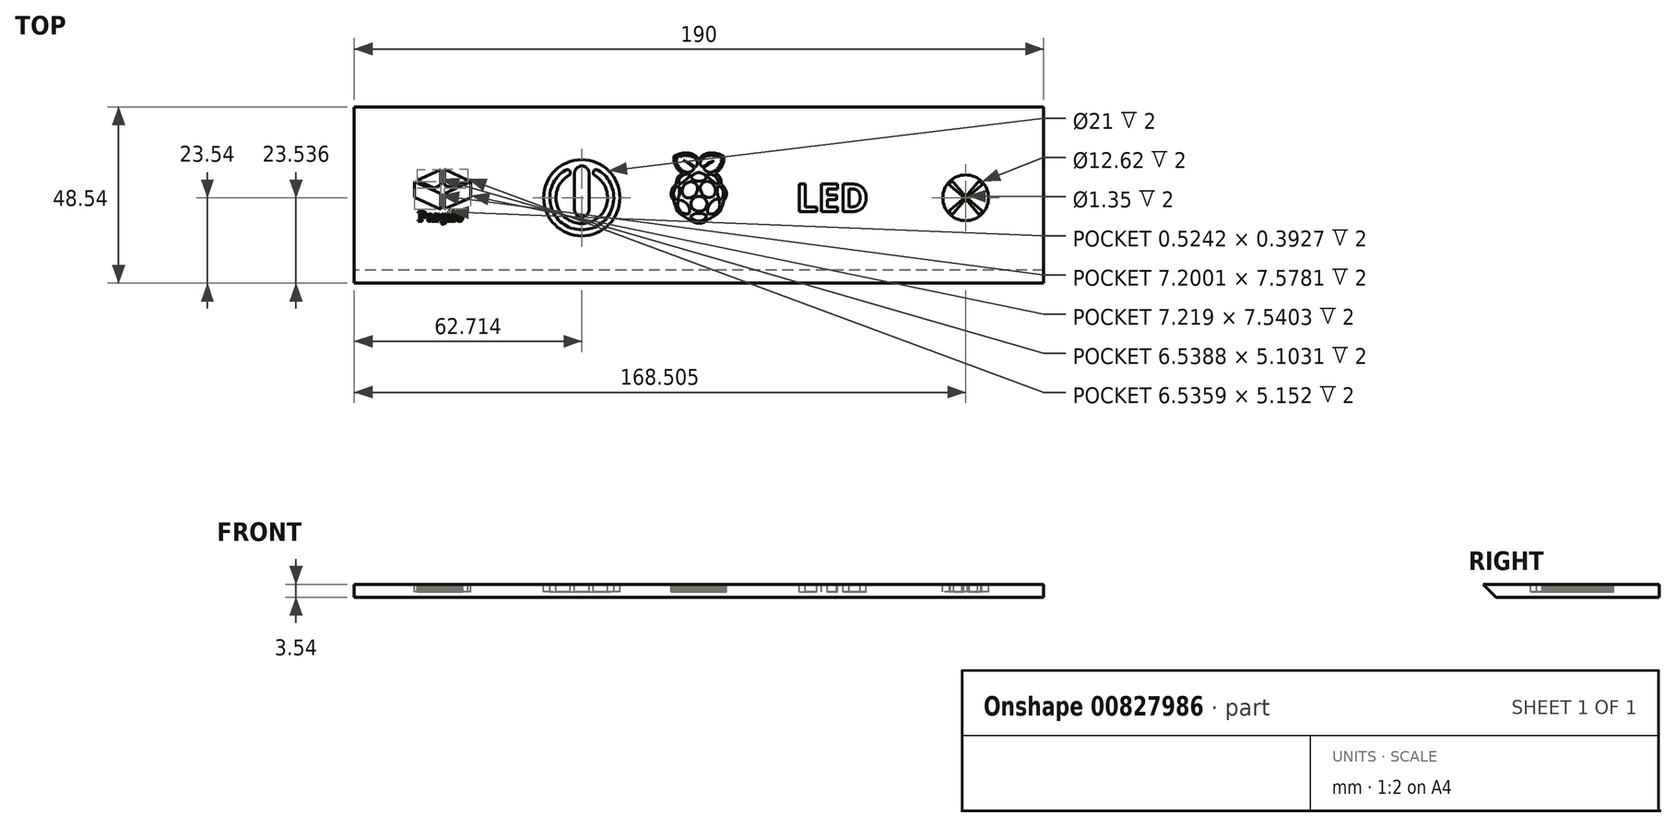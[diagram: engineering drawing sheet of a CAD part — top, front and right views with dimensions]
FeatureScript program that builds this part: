
annotation { "Feature Type Name" : "Feature", "Feature Type Description" : "" }
export const myFeature = defineFeature(function(context is Context, id is Id, definition is map)
    precondition{}
    {
        {
            var Q0;
            Q0=qCreatedBy(makeId("Top.planeOp"),FACE);
            var sketch = newSketch(context, id + "F0", { "sketchPlane" : qUnion([Q0])});
            skLineSegment(sketch, "E0.bottom", {"start": v(95, -25) * mm, "end": v(-95, -25) * mm});
            skLineSegment(sketch, "E0.top", {"start": v(95, 25) * mm, "end": v(-95, 25) * mm});
            skLineSegment(sketch, "E0.left", {"start": v(95, -25) * mm, "end": v(95, 25) * mm});
            skLineSegment(sketch, "E0.right", {"start": v(-95, -25) * mm, "end": v(-95, 25) * mm});
            skPoint(sketch, "E1.endSnap0", {"position": v(-58.55, -14.96) * mm});
            skSolve(sketch);
        }
        {
            var Q0;
            Q0=makeQuery(id+"F0.imprint","IMPRINT",FACE,{"disambiguationData":[TD([[makeQuery(id+"F0.imprint","IMPRINT",EDGE,{"derivedFrom":sQuery(id+"F0.wireOp",EDGE,"E0.bottom")}),-1.0]])]});
            extrude(context, id + "F1", {"entities" : qUnion([Q0]), "depth" : 3.54 * mm, "offsetDistance" : 25 * mm});
        }
        {
            var Q0;
            Q0=makeQuery(id+"F1.opExtrude","CAP_EDGE",EDGE,{"disambiguationData":[OSD([sQuery(id+"F0.wireOp",EDGE,"E0.bottom")])],"isStart":true});
            chamfer(context, id + "F2", {"entities" : qUnion([Q0]), "width" : 5 * mm, "tangentPropagation" : true});
        }
        {
            var Q0;
            Q0=makeQuery(id+"F1.opExtrude","CAP_FACE",FACE,{"disambiguationData":[OSD([sQuery(id+"F0.wireOp",EDGE,"E0.bottom"),sQuery(id+"F0.wireOp",EDGE,"E0.top"),sQuery(id+"F0.wireOp",EDGE,"E0.left"),sQuery(id+"F0.wireOp",EDGE,"E0.right")])],"isStart":false});
            var sketch = newSketch(context, id + "F3", { "sketchPlane" : qUnion([Q0])});
            skPoint(sketch, "E2", {"position": v(0, 6.13) * mm});
            skPoint(sketch, "E3", {"position": v(36.75, 0) * mm});
            skPoint(sketch, "E4", {"position": v(73.5, 0) * mm});
            skPoint(sketch, "E5", {"position": v(-70.53, 0) * mm});
            skPoint(sketch, "E6", {"position": v(-32.17, -0.8) * mm});
            skLineSegment(sketch, "E7", {"start": v(0.77, -6.95) * mm, "end": v(0.42, -7.01) * mm});
            skLineSegment(sketch, "E8", {"start": v(0.42, -7.01) * mm, "end": v(0.04, -7.03) * mm});
            skLineSegment(sketch, "E9", {"start": v(2.22, -6.14) * mm, "end": v(1.83, -6.45) * mm});
            skLineSegment(sketch, "E10", {"start": v(1.83, -6.45) * mm, "end": v(1.43, -6.7) * mm});
            skLineSegment(sketch, "E11", {"start": v(1.43, -6.7) * mm, "end": v(0.77, -6.95) * mm});
            skLineSegment(sketch, "E12", {"start": v(2.72, -5.84) * mm, "end": v(2.42, -6) * mm});
            skLineSegment(sketch, "E13", {"start": v(2.42, -6) * mm, "end": v(2.22, -6.14) * mm});
            skLineSegment(sketch, "E14", {"start": v(3.97, -5.13) * mm, "end": v(3.25, -5.58) * mm});
            skLineSegment(sketch, "E15", {"start": v(3.25, -5.58) * mm, "end": v(2.72, -5.84) * mm});
            skLineSegment(sketch, "E16", {"start": v(4.55, -4.78) * mm, "end": v(4.42, -4.85) * mm});
            skLineSegment(sketch, "E17", {"start": v(4.42, -4.85) * mm, "end": v(4.25, -4.95) * mm});
            skLineSegment(sketch, "E18", {"start": v(4.25, -4.95) * mm, "end": v(3.97, -5.13) * mm});
            skLineSegment(sketch, "E19", {"start": v(5.47, -4.1) * mm, "end": v(5.2, -4.35) * mm});
            skLineSegment(sketch, "E20", {"start": v(5.2, -4.35) * mm, "end": v(4.96, -4.54) * mm});
            skLineSegment(sketch, "E21", {"start": v(4.96, -4.54) * mm, "end": v(4.55, -4.78) * mm});
            skLineSegment(sketch, "E22", {"start": v(6.36, -2.47) * mm, "end": v(6.2, -2.98) * mm});
            skLineSegment(sketch, "E23", {"start": v(6.2, -2.98) * mm, "end": v(5.98, -3.45) * mm});
            skLineSegment(sketch, "E24", {"start": v(5.98, -3.45) * mm, "end": v(5.75, -3.8) * mm});
            skLineSegment(sketch, "E25", {"start": v(5.75, -3.8) * mm, "end": v(5.47, -4.1) * mm});
            skLineSegment(sketch, "E26", {"start": v(6.55, -1.8) * mm, "end": v(6.42, -2.2) * mm});
            skLineSegment(sketch, "E27", {"start": v(6.42, -2.2) * mm, "end": v(6.36, -2.47) * mm});
            skLineSegment(sketch, "E28", {"start": v(6.75, -1.16) * mm, "end": v(6.7, -1.31) * mm});
            skLineSegment(sketch, "E29", {"start": v(6.7, -1.31) * mm, "end": v(6.65, -1.5) * mm});
            skLineSegment(sketch, "E30", {"start": v(6.65, -1.5) * mm, "end": v(6.55, -1.8) * mm});
            skLineSegment(sketch, "E31", {"start": v(6.98, -0.7) * mm, "end": v(6.89, -0.82) * mm});
            skLineSegment(sketch, "E32", {"start": v(6.89, -0.82) * mm, "end": v(6.82, -0.94) * mm});
            skLineSegment(sketch, "E33", {"start": v(6.82, -0.94) * mm, "end": v(6.75, -1.16) * mm});
            skLineSegment(sketch, "E34", {"start": v(7.5, 0.37) * mm, "end": v(7.4, 0.07) * mm});
            skLineSegment(sketch, "E35", {"start": v(7.4, 0.07) * mm, "end": v(7.25, -0.25) * mm});
            skLineSegment(sketch, "E36", {"start": v(7.25, -0.25) * mm, "end": v(7.12, -0.49) * mm});
            skLineSegment(sketch, "E37", {"start": v(7.12, -0.49) * mm, "end": v(6.98, -0.7) * mm});
            skLineSegment(sketch, "E38", {"start": v(7.5, 1.8) * mm, "end": v(7.56, 1.42) * mm});
            skLineSegment(sketch, "E39", {"start": v(7.56, 1.42) * mm, "end": v(7.57, 0.99) * mm});
            skLineSegment(sketch, "E40", {"start": v(7.57, 0.99) * mm, "end": v(7.55, 0.65) * mm});
            skLineSegment(sketch, "E41", {"start": v(7.55, 0.65) * mm, "end": v(7.5, 0.37) * mm});
            skLineSegment(sketch, "E42", {"start": v(7.13, 2.68) * mm, "end": v(7.37, 2.2) * mm});
            skLineSegment(sketch, "E43", {"start": v(7.37, 2.2) * mm, "end": v(7.5, 1.8) * mm});
            skLineSegment(sketch, "E44", {"start": v(6.4, 3.5) * mm, "end": v(6.6, 3.33) * mm});
            skLineSegment(sketch, "E45", {"start": v(6.6, 3.33) * mm, "end": v(6.84, 3.08) * mm});
            skLineSegment(sketch, "E46", {"start": v(6.84, 3.08) * mm, "end": v(7, 2.87) * mm});
            skLineSegment(sketch, "E47", {"start": v(7, 2.87) * mm, "end": v(7.13, 2.68) * mm});
            skLineSegment(sketch, "E48", {"start": v(6.12, 4.2) * mm, "end": v(6.15, 3.9) * mm});
            skLineSegment(sketch, "E49", {"start": v(6.15, 3.9) * mm, "end": v(6.2, 3.71) * mm});
            skLineSegment(sketch, "E50", {"start": v(6.2, 3.71) * mm, "end": v(6.4, 3.5) * mm});
            skLineSegment(sketch, "E51", {"start": v(4.66, 6.7) * mm, "end": v(5.12, 6.35) * mm});
            skLineSegment(sketch, "E52", {"start": v(5.12, 6.35) * mm, "end": v(5.5, 5.95) * mm});
            skLineSegment(sketch, "E53", {"start": v(5.5, 5.95) * mm, "end": v(5.8, 5.5) * mm});
            skLineSegment(sketch, "E54", {"start": v(5.8, 5.5) * mm, "end": v(6.02, 4.89) * mm});
            skLineSegment(sketch, "E55", {"start": v(6.02, 4.89) * mm, "end": v(6.12, 4.2) * mm});
            skLineSegment(sketch, "E56", {"start": v(4.5, 6.8) * mm, "end": v(4.66, 6.7) * mm});
            skLineSegment(sketch, "E57", {"start": v(4.7, 6.88) * mm, "end": v(4.5, 6.8) * mm});
            skLineSegment(sketch, "E58", {"start": v(5.04, 7.22) * mm, "end": v(4.9, 7) * mm});
            skLineSegment(sketch, "E59", {"start": v(4.9, 7) * mm, "end": v(4.7, 6.88) * mm});
            skLineSegment(sketch, "E60", {"start": v(5.23, 7.35) * mm, "end": v(5.09, 7.28) * mm});
            skLineSegment(sketch, "E61", {"start": v(5.09, 7.28) * mm, "end": v(5.04, 7.22) * mm});
            skLineSegment(sketch, "E62", {"start": v(5.67, 7.78) * mm, "end": v(5.6, 7.63) * mm});
            skLineSegment(sketch, "E63", {"start": v(5.6, 7.63) * mm, "end": v(5.48, 7.5) * mm});
            skLineSegment(sketch, "E64", {"start": v(5.48, 7.5) * mm, "end": v(5.23, 7.35) * mm});
            skLineSegment(sketch, "E65", {"start": v(5.8, 7.95) * mm, "end": v(5.71, 7.87) * mm});
            skLineSegment(sketch, "E66", {"start": v(5.71, 7.87) * mm, "end": v(5.67, 7.78) * mm});
            skLineSegment(sketch, "E67", {"start": v(6.2, 8.49) * mm, "end": v(6.13, 8.32) * mm});
            skLineSegment(sketch, "E68", {"start": v(6.13, 8.32) * mm, "end": v(6.01, 8.15) * mm});
            skLineSegment(sketch, "E69", {"start": v(6.01, 8.15) * mm, "end": v(5.8, 7.95) * mm});
            skLineSegment(sketch, "E70", {"start": v(6.3, 8.7) * mm, "end": v(6.26, 8.66) * mm});
            skLineSegment(sketch, "E71", {"start": v(6.26, 8.66) * mm, "end": v(6.24, 8.61) * mm});
            skLineSegment(sketch, "E72", {"start": v(6.24, 8.61) * mm, "end": v(6.2, 8.49) * mm});
            skLineSegment(sketch, "E73", {"start": v(6.52, 9.16) * mm, "end": v(6.5, 9.01) * mm});
            skLineSegment(sketch, "E74", {"start": v(6.5, 9.01) * mm, "end": v(6.43, 8.86) * mm});
            skLineSegment(sketch, "E75", {"start": v(6.43, 8.86) * mm, "end": v(6.37, 8.76) * mm});
            skLineSegment(sketch, "E76", {"start": v(6.37, 8.76) * mm, "end": v(6.3, 8.7) * mm});
            skLineSegment(sketch, "E77", {"start": v(6.63, 9.47) * mm, "end": v(6.54, 9.3) * mm});
            skLineSegment(sketch, "E78", {"start": v(6.54, 9.3) * mm, "end": v(6.52, 9.16) * mm});
            skLineSegment(sketch, "E79", {"start": v(6.77, 9.96) * mm, "end": v(6.75, 9.7) * mm});
            skLineSegment(sketch, "E80", {"start": v(6.75, 9.7) * mm, "end": v(6.63, 9.47) * mm});
            skLineSegment(sketch, "E81", {"start": v(6.83, 10.21) * mm, "end": v(6.77, 10.06) * mm});
            skLineSegment(sketch, "E82", {"start": v(6.77, 10.06) * mm, "end": v(6.77, 9.96) * mm});
            skLineSegment(sketch, "E83", {"start": v(6.85, 10.75) * mm, "end": v(6.9, 10.45) * mm});
            skLineSegment(sketch, "E84", {"start": v(6.9, 10.45) * mm, "end": v(6.83, 10.21) * mm});
            skLineSegment(sketch, "E85", {"start": v(6.81, 10.96) * mm, "end": v(6.8, 10.86) * mm});
            skLineSegment(sketch, "E86", {"start": v(6.8, 10.86) * mm, "end": v(6.85, 10.75) * mm});
            skLineSegment(sketch, "E87", {"start": v(6.78, 11.48) * mm, "end": v(6.82, 11.35) * mm});
            skLineSegment(sketch, "E88", {"start": v(6.82, 11.35) * mm, "end": v(6.84, 11.2) * mm});
            skLineSegment(sketch, "E89", {"start": v(6.84, 11.2) * mm, "end": v(6.81, 10.96) * mm});
            skLineSegment(sketch, "E90", {"start": v(6.29, 11.71) * mm, "end": v(6.6, 11.63) * mm});
            skLineSegment(sketch, "E91", {"start": v(6.6, 11.63) * mm, "end": v(6.78, 11.48) * mm});
            skLineSegment(sketch, "E92", {"start": v(6.08, 11.78) * mm, "end": v(6.17, 11.73) * mm});
            skLineSegment(sketch, "E93", {"start": v(6.17, 11.73) * mm, "end": v(6.29, 11.71) * mm});
            skLineSegment(sketch, "E94", {"start": v(5.5, 12) * mm, "end": v(5.88, 11.92) * mm});
            skLineSegment(sketch, "E95", {"start": v(5.88, 11.92) * mm, "end": v(6.08, 11.78) * mm});
            skLineSegment(sketch, "E96", {"start": v(5.18, 12.06) * mm, "end": v(5.24, 12.04) * mm});
            skLineSegment(sketch, "E97", {"start": v(5.24, 12.04) * mm, "end": v(5.31, 12.02) * mm});
            skLineSegment(sketch, "E98", {"start": v(5.31, 12.02) * mm, "end": v(5.5, 12) * mm});
            skLineSegment(sketch, "E99", {"start": v(4.75, 12.2) * mm, "end": v(5.02, 12.15) * mm});
            skLineSegment(sketch, "E100", {"start": v(5.02, 12.15) * mm, "end": v(5.18, 12.06) * mm});
            skLineSegment(sketch, "E101", {"start": v(4.5, 12.27) * mm, "end": v(4.64, 12.22) * mm});
            skLineSegment(sketch, "E102", {"start": v(4.64, 12.22) * mm, "end": v(4.75, 12.2) * mm});
            skLineSegment(sketch, "E103", {"start": v(3.87, 12.3) * mm, "end": v(4.03, 12.33) * mm});
            skLineSegment(sketch, "E104", {"start": v(4.03, 12.33) * mm, "end": v(4.23, 12.33) * mm});
            skLineSegment(sketch, "E105", {"start": v(4.23, 12.33) * mm, "end": v(4.37, 12.3) * mm});
            skLineSegment(sketch, "E106", {"start": v(4.37, 12.3) * mm, "end": v(4.5, 12.27) * mm});
            skLineSegment(sketch, "E107", {"start": v(3.7, 12.32) * mm, "end": v(3.8, 12.28) * mm});
            skLineSegment(sketch, "E108", {"start": v(3.8, 12.28) * mm, "end": v(3.87, 12.3) * mm});
            skLineSegment(sketch, "E109", {"start": v(3.12, 12.31) * mm, "end": v(3.27, 12.35) * mm});
            skLineSegment(sketch, "E110", {"start": v(3.27, 12.35) * mm, "end": v(3.46, 12.36) * mm});
            skLineSegment(sketch, "E111", {"start": v(3.46, 12.36) * mm, "end": v(3.6, 12.35) * mm});
            skLineSegment(sketch, "E112", {"start": v(3.6, 12.35) * mm, "end": v(3.7, 12.32) * mm});
            skLineSegment(sketch, "E113", {"start": v(2.74, 12.26) * mm, "end": v(2.99, 12.28) * mm});
            skLineSegment(sketch, "E114", {"start": v(2.99, 12.28) * mm, "end": v(3.12, 12.31) * mm});
            skLineSegment(sketch, "E115", {"start": v(2.34, 12.19) * mm, "end": v(2.53, 12.26) * mm});
            skLineSegment(sketch, "E116", {"start": v(2.53, 12.26) * mm, "end": v(2.74, 12.26) * mm});
            skLineSegment(sketch, "E117", {"start": v(2.08, 12.12) * mm, "end": v(2.22, 12.13) * mm});
            skLineSegment(sketch, "E118", {"start": v(2.22, 12.13) * mm, "end": v(2.34, 12.19) * mm});
            skLineSegment(sketch, "E119", {"start": v(1.52, 11.92) * mm, "end": v(1.83, 12.1) * mm});
            skLineSegment(sketch, "E120", {"start": v(1.83, 12.1) * mm, "end": v(2.08, 12.12) * mm});
            skLineSegment(sketch, "E121", {"start": v(1.24, 11.78) * mm, "end": v(1.39, 11.81) * mm});
            skLineSegment(sketch, "E122", {"start": v(1.39, 11.81) * mm, "end": v(1.52, 11.92) * mm});
            skLineSegment(sketch, "E123", {"start": v(0.07, 10.47) * mm, "end": v(0.35, 11.02) * mm});
            skLineSegment(sketch, "E124", {"start": v(0.35, 11.02) * mm, "end": v(0.7, 11.46) * mm});
            skLineSegment(sketch, "E125", {"start": v(0.7, 11.46) * mm, "end": v(1.02, 11.71) * mm});
            skLineSegment(sketch, "E126", {"start": v(1.02, 11.71) * mm, "end": v(1.24, 11.78) * mm});
            skLineSegment(sketch, "E127", {"start": v(-0.07, 10.3) * mm, "end": v(-0.07, 10.27) * mm});
            skLineSegment(sketch, "E128", {"start": v(-0.07, 10.27) * mm, "end": v(-0.06, 10.26) * mm});
            skLineSegment(sketch, "E129", {"start": v(-0.06, 10.26) * mm, "end": v(-0.05, 10.25) * mm});
            skLineSegment(sketch, "E130", {"start": v(-0.05, 10.25) * mm, "end": v(-0.04, 10.26) * mm});
            skLineSegment(sketch, "E131", {"start": v(-0.04, 10.26) * mm, "end": v(0.01, 10.35) * mm});
            skLineSegment(sketch, "E132", {"start": v(0.01, 10.35) * mm, "end": v(0.07, 10.47) * mm});
            skLineSegment(sketch, "E133", {"start": v(-0.6, 11.27) * mm, "end": v(-0.5, 11.11) * mm});
            skLineSegment(sketch, "E134", {"start": v(-0.5, 11.11) * mm, "end": v(-0.36, 10.9) * mm});
            skLineSegment(sketch, "E135", {"start": v(-0.36, 10.9) * mm, "end": v(-0.23, 10.67) * mm});
            skLineSegment(sketch, "E136", {"start": v(-0.23, 10.67) * mm, "end": v(-0.1, 10.42) * mm});
            skLineSegment(sketch, "E137", {"start": v(-0.1, 10.42) * mm, "end": v(-0.08, 10.34) * mm});
            skLineSegment(sketch, "E138", {"start": v(-0.08, 10.34) * mm, "end": v(-0.07, 10.3) * mm});
            skLineSegment(sketch, "E139", {"start": v(-1.31, 11.78) * mm, "end": v(-1.14, 11.73) * mm});
            skLineSegment(sketch, "E140", {"start": v(-1.14, 11.73) * mm, "end": v(-0.94, 11.6) * mm});
            skLineSegment(sketch, "E141", {"start": v(-0.94, 11.6) * mm, "end": v(-0.6, 11.27) * mm});
            skLineSegment(sketch, "E142", {"start": v(-1.6, 11.92) * mm, "end": v(-1.5, 11.84) * mm});
            skLineSegment(sketch, "E143", {"start": v(-1.5, 11.84) * mm, "end": v(-1.43, 11.8) * mm});
            skLineSegment(sketch, "E144", {"start": v(-1.43, 11.8) * mm, "end": v(-1.31, 11.78) * mm});
            skLineSegment(sketch, "E145", {"start": v(-2.14, 12.13) * mm, "end": v(-1.83, 12.08) * mm});
            skLineSegment(sketch, "E146", {"start": v(-1.83, 12.08) * mm, "end": v(-1.6, 11.92) * mm});
            skLineSegment(sketch, "E147", {"start": v(-2.42, 12.2) * mm, "end": v(-2.25, 12.13) * mm});
            skLineSegment(sketch, "E148", {"start": v(-2.25, 12.13) * mm, "end": v(-2.14, 12.13) * mm});
            skLineSegment(sketch, "E149", {"start": v(-2.8, 12.26) * mm, "end": v(-2.67, 12.26) * mm});
            skLineSegment(sketch, "E150", {"start": v(-2.67, 12.26) * mm, "end": v(-2.57, 12.25) * mm});
            skLineSegment(sketch, "E151", {"start": v(-2.57, 12.25) * mm, "end": v(-2.42, 12.2) * mm});
            skLineSegment(sketch, "E152", {"start": v(-3.16, 12.3) * mm, "end": v(-2.98, 12.26) * mm});
            skLineSegment(sketch, "E153", {"start": v(-2.98, 12.26) * mm, "end": v(-2.8, 12.26) * mm});
            skLineSegment(sketch, "E154", {"start": v(-3.77, 12.32) * mm, "end": v(-3.62, 12.36) * mm});
            skLineSegment(sketch, "E155", {"start": v(-3.62, 12.36) * mm, "end": v(-3.43, 12.36) * mm});
            skLineSegment(sketch, "E156", {"start": v(-3.43, 12.36) * mm, "end": v(-3.16, 12.3) * mm});
            skLineSegment(sketch, "E157", {"start": v(-3.96, 12.3) * mm, "end": v(-3.85, 12.29) * mm});
            skLineSegment(sketch, "E158", {"start": v(-3.85, 12.29) * mm, "end": v(-3.77, 12.32) * mm});
            skLineSegment(sketch, "E159", {"start": v(-4.6, 12.25) * mm, "end": v(-4.43, 12.3) * mm});
            skLineSegment(sketch, "E160", {"start": v(-4.43, 12.3) * mm, "end": v(-4.25, 12.33) * mm});
            skLineSegment(sketch, "E161", {"start": v(-4.25, 12.33) * mm, "end": v(-4.09, 12.33) * mm});
            skLineSegment(sketch, "E162", {"start": v(-4.09, 12.33) * mm, "end": v(-3.96, 12.3) * mm});
            skLineSegment(sketch, "E163", {"start": v(-4.8, 12.2) * mm, "end": v(-4.68, 12.21) * mm});
            skLineSegment(sketch, "E164", {"start": v(-4.68, 12.21) * mm, "end": v(-4.6, 12.25) * mm});
            skLineSegment(sketch, "E165", {"start": v(-5.24, 12.07) * mm, "end": v(-5, 12.18) * mm});
            skLineSegment(sketch, "E166", {"start": v(-5, 12.18) * mm, "end": v(-4.8, 12.2) * mm});
            skLineSegment(sketch, "E167", {"start": v(-5.51, 12) * mm, "end": v(-5.33, 12.03) * mm});
            skLineSegment(sketch, "E168", {"start": v(-5.33, 12.03) * mm, "end": v(-5.24, 12.07) * mm});
            skLineSegment(sketch, "E169", {"start": v(-6.09, 11.83) * mm, "end": v(-5.8, 11.98) * mm});
            skLineSegment(sketch, "E170", {"start": v(-5.8, 11.98) * mm, "end": v(-5.51, 12) * mm});
            skLineSegment(sketch, "E171", {"start": v(-6.37, 11.71) * mm, "end": v(-6.22, 11.75) * mm});
            skLineSegment(sketch, "E172", {"start": v(-6.22, 11.75) * mm, "end": v(-6.09, 11.83) * mm});
            skLineSegment(sketch, "E173", {"start": v(-6.85, 11.48) * mm, "end": v(-6.76, 11.58) * mm});
            skLineSegment(sketch, "E174", {"start": v(-6.76, 11.58) * mm, "end": v(-6.62, 11.66) * mm});
            skLineSegment(sketch, "E175", {"start": v(-6.62, 11.66) * mm, "end": v(-6.37, 11.71) * mm});
            skLineSegment(sketch, "E176", {"start": v(-6.89, 10.95) * mm, "end": v(-6.92, 11.1) * mm});
            skLineSegment(sketch, "E177", {"start": v(-6.92, 11.1) * mm, "end": v(-6.91, 11.26) * mm});
            skLineSegment(sketch, "E178", {"start": v(-6.91, 11.26) * mm, "end": v(-6.85, 11.48) * mm});
            skLineSegment(sketch, "E179", {"start": v(-6.92, 10.74) * mm, "end": v(-6.87, 10.87) * mm});
            skLineSegment(sketch, "E180", {"start": v(-6.87, 10.87) * mm, "end": v(-6.89, 10.95) * mm});
            skLineSegment(sketch, "E181", {"start": v(-6.9, 10.22) * mm, "end": v(-6.98, 10.52) * mm});
            skLineSegment(sketch, "E182", {"start": v(-6.98, 10.52) * mm, "end": v(-6.92, 10.74) * mm});
            skLineSegment(sketch, "E183", {"start": v(-6.84, 9.95) * mm, "end": v(-6.84, 10.08) * mm});
            skLineSegment(sketch, "E184", {"start": v(-6.84, 10.08) * mm, "end": v(-6.9, 10.22) * mm});
            skLineSegment(sketch, "E185", {"start": v(-6.69, 9.45) * mm, "end": v(-6.83, 9.75) * mm});
            skLineSegment(sketch, "E186", {"start": v(-6.83, 9.75) * mm, "end": v(-6.84, 9.95) * mm});
            skLineSegment(sketch, "E187", {"start": v(-6.6, 9.18) * mm, "end": v(-6.62, 9.33) * mm});
            skLineSegment(sketch, "E188", {"start": v(-6.62, 9.33) * mm, "end": v(-6.69, 9.45) * mm});
            skLineSegment(sketch, "E189", {"start": v(-6.39, 8.73) * mm, "end": v(-6.55, 8.97) * mm});
            skLineSegment(sketch, "E190", {"start": v(-6.55, 8.97) * mm, "end": v(-6.6, 9.18) * mm});
            skLineSegment(sketch, "E191", {"start": v(-6.27, 8.53) * mm, "end": v(-6.3, 8.64) * mm});
            skLineSegment(sketch, "E192", {"start": v(-6.3, 8.64) * mm, "end": v(-6.39, 8.73) * mm});
            skLineSegment(sketch, "E193", {"start": v(-5.82, 7.92) * mm, "end": v(-6, 8.06) * mm});
            skLineSegment(sketch, "E194", {"start": v(-6, 8.06) * mm, "end": v(-6.16, 8.24) * mm});
            skLineSegment(sketch, "E195", {"start": v(-6.16, 8.24) * mm, "end": v(-6.24, 8.4) * mm});
            skLineSegment(sketch, "E196", {"start": v(-6.24, 8.4) * mm, "end": v(-6.27, 8.53) * mm});
            skLineSegment(sketch, "E197", {"start": v(-5.75, 7.83) * mm, "end": v(-5.77, 7.89) * mm});
            skLineSegment(sketch, "E198", {"start": v(-5.77, 7.89) * mm, "end": v(-5.82, 7.92) * mm});
            skLineSegment(sketch, "E199", {"start": v(-5.23, 7.32) * mm, "end": v(-5.43, 7.4) * mm});
            skLineSegment(sketch, "E200", {"start": v(-5.43, 7.4) * mm, "end": v(-5.61, 7.56) * mm});
            skLineSegment(sketch, "E201", {"start": v(-5.61, 7.56) * mm, "end": v(-5.71, 7.7) * mm});
            skLineSegment(sketch, "E202", {"start": v(-5.71, 7.7) * mm, "end": v(-5.75, 7.83) * mm});
            skLineSegment(sketch, "E203", {"start": v(-5.08, 7.16) * mm, "end": v(-5.16, 7.28) * mm});
            skLineSegment(sketch, "E204", {"start": v(-5.16, 7.28) * mm, "end": v(-5.23, 7.32) * mm});
            skLineSegment(sketch, "E205", {"start": v(-4.64, 6.83) * mm, "end": v(-4.8, 6.89) * mm});
            skLineSegment(sketch, "E206", {"start": v(-4.8, 6.89) * mm, "end": v(-4.93, 6.98) * mm});
            skLineSegment(sketch, "E207", {"start": v(-4.93, 6.98) * mm, "end": v(-5.08, 7.16) * mm});
            skLineSegment(sketch, "E208", {"start": v(-4.84, 6.62) * mm, "end": v(-4.65, 6.75) * mm});
            skLineSegment(sketch, "E209", {"start": v(-4.65, 6.75) * mm, "end": v(-4.6, 6.8) * mm});
            skLineSegment(sketch, "E210", {"start": v(-4.6, 6.8) * mm, "end": v(-4.6, 6.8) * mm});
            skLineSegment(sketch, "E211", {"start": v(-4.6, 6.8) * mm, "end": v(-4.6, 6.81) * mm});
            skLineSegment(sketch, "E212", {"start": v(-4.6, 6.81) * mm, "end": v(-4.62, 6.82) * mm});
            skLineSegment(sketch, "E213", {"start": v(-4.62, 6.82) * mm, "end": v(-4.64, 6.83) * mm});
            skLineSegment(sketch, "E214", {"start": v(-5.76, 5.7) * mm, "end": v(-5.56, 5.96) * mm});
            skLineSegment(sketch, "E215", {"start": v(-5.56, 5.96) * mm, "end": v(-5.3, 6.24) * mm});
            skLineSegment(sketch, "E216", {"start": v(-5.3, 6.24) * mm, "end": v(-5.06, 6.45) * mm});
            skLineSegment(sketch, "E217", {"start": v(-5.06, 6.45) * mm, "end": v(-4.84, 6.62) * mm});
            skLineSegment(sketch, "E218", {"start": v(-6.2, 4.15) * mm, "end": v(-6.14, 4.64) * mm});
            skLineSegment(sketch, "E219", {"start": v(-6.14, 4.64) * mm, "end": v(-6.04, 5.08) * mm});
            skLineSegment(sketch, "E220", {"start": v(-6.04, 5.08) * mm, "end": v(-5.76, 5.7) * mm});
            skLineSegment(sketch, "E221", {"start": v(-6.5, 3.5) * mm, "end": v(-6.34, 3.62) * mm});
            skLineSegment(sketch, "E222", {"start": v(-6.34, 3.62) * mm, "end": v(-6.25, 3.77) * mm});
            skLineSegment(sketch, "E223", {"start": v(-6.25, 3.77) * mm, "end": v(-6.21, 3.93) * mm});
            skLineSegment(sketch, "E224", {"start": v(-6.21, 3.93) * mm, "end": v(-6.2, 4.15) * mm});
            skLineSegment(sketch, "E225", {"start": v(-7.57, 1.76) * mm, "end": v(-7.37, 2.34) * mm});
            skLineSegment(sketch, "E226", {"start": v(-7.37, 2.34) * mm, "end": v(-7.08, 2.86) * mm});
            skLineSegment(sketch, "E227", {"start": v(-7.08, 2.86) * mm, "end": v(-6.8, 3.21) * mm});
            skLineSegment(sketch, "E228", {"start": v(-6.8, 3.21) * mm, "end": v(-6.5, 3.5) * mm});
            skLineSegment(sketch, "E229", {"start": v(-7.57, 0.39) * mm, "end": v(-7.63, 0.75) * mm});
            skLineSegment(sketch, "E230", {"start": v(-7.63, 0.75) * mm, "end": v(-7.65, 1.16) * mm});
            skLineSegment(sketch, "E231", {"start": v(-7.65, 1.16) * mm, "end": v(-7.62, 1.47) * mm});
            skLineSegment(sketch, "E232", {"start": v(-7.62, 1.47) * mm, "end": v(-7.57, 1.76) * mm});
            skLineSegment(sketch, "E233", {"start": v(-7.07, -0.66) * mm, "end": v(-7.4, -0.09) * mm});
            skLineSegment(sketch, "E234", {"start": v(-7.4, -0.09) * mm, "end": v(-7.57, 0.39) * mm});
            skLineSegment(sketch, "E235", {"start": v(-6.8, -1.22) * mm, "end": v(-6.86, -1.04) * mm});
            skLineSegment(sketch, "E236", {"start": v(-6.86, -1.04) * mm, "end": v(-6.92, -0.9) * mm});
            skLineSegment(sketch, "E237", {"start": v(-6.92, -0.9) * mm, "end": v(-7.07, -0.66) * mm});
            skLineSegment(sketch, "E238", {"start": v(-6.6, -1.84) * mm, "end": v(-6.73, -1.48) * mm});
            skLineSegment(sketch, "E239", {"start": v(-6.73, -1.48) * mm, "end": v(-6.8, -1.22) * mm});
            skLineSegment(sketch, "E240", {"start": v(-6.43, -2.47) * mm, "end": v(-6.47, -2.3) * mm});
            skLineSegment(sketch, "E241", {"start": v(-6.47, -2.3) * mm, "end": v(-6.52, -2.11) * mm});
            skLineSegment(sketch, "E242", {"start": v(-6.52, -2.11) * mm, "end": v(-6.6, -1.84) * mm});
            skLineSegment(sketch, "E243", {"start": v(-4.62, -4.78) * mm, "end": v(-5.1, -4.5) * mm});
            skLineSegment(sketch, "E244", {"start": v(-5.1, -4.5) * mm, "end": v(-5.53, -4.14) * mm});
            skLineSegment(sketch, "E245", {"start": v(-5.53, -4.14) * mm, "end": v(-5.89, -3.7) * mm});
            skLineSegment(sketch, "E246", {"start": v(-5.89, -3.7) * mm, "end": v(-6.22, -3.12) * mm});
            skLineSegment(sketch, "E247", {"start": v(-6.22, -3.12) * mm, "end": v(-6.43, -2.47) * mm});
            skLineSegment(sketch, "E248", {"start": v(-4.14, -5.07) * mm, "end": v(-4.42, -4.89) * mm});
            skLineSegment(sketch, "E249", {"start": v(-4.42, -4.89) * mm, "end": v(-4.62, -4.78) * mm});
            skLineSegment(sketch, "E250", {"start": v(-2.81, -5.83) * mm, "end": v(-3.17, -5.66) * mm});
            skLineSegment(sketch, "E251", {"start": v(-3.17, -5.66) * mm, "end": v(-3.55, -5.45) * mm});
            skLineSegment(sketch, "E252", {"start": v(-3.55, -5.45) * mm, "end": v(-4.14, -5.07) * mm});
            skLineSegment(sketch, "E253", {"start": v(-2.26, -6.17) * mm, "end": v(-2.52, -5.97) * mm});
            skLineSegment(sketch, "E254", {"start": v(-2.52, -5.97) * mm, "end": v(-2.65, -5.9) * mm});
            skLineSegment(sketch, "E255", {"start": v(-2.65, -5.9) * mm, "end": v(-2.81, -5.83) * mm});
            skLineSegment(sketch, "E256", {"start": v(-0.5, -7.02) * mm, "end": v(-1.04, -6.9) * mm});
            skLineSegment(sketch, "E257", {"start": v(-1.04, -6.9) * mm, "end": v(-1.55, -6.67) * mm});
            skLineSegment(sketch, "E258", {"start": v(-1.55, -6.67) * mm, "end": v(-1.92, -6.44) * mm});
            skLineSegment(sketch, "E259", {"start": v(-1.92, -6.44) * mm, "end": v(-2.26, -6.17) * mm});
            skLineSegment(sketch, "E260", {"start": v(0.04, -7.03) * mm, "end": v(-0.16, -7.03) * mm});
            skLineSegment(sketch, "E261", {"start": v(-0.16, -7.03) * mm, "end": v(-0.34, -7.03) * mm});
            skLineSegment(sketch, "E262", {"start": v(-0.34, -7.03) * mm, "end": v(-0.45, -7.03) * mm});
            skLineSegment(sketch, "E263", {"start": v(-0.45, -7.03) * mm, "end": v(-0.5, -7.02) * mm});
            skLineSegment(sketch, "E264", {"start": v(1.43, -5.93) * mm, "end": v(1.01, -6.18) * mm});
            skLineSegment(sketch, "E265", {"start": v(1.01, -6.18) * mm, "end": v(0.6, -6.34) * mm});
            skLineSegment(sketch, "E266", {"start": v(0.6, -6.34) * mm, "end": v(0.27, -6.4) * mm});
            skLineSegment(sketch, "E267", {"start": v(0.27, -6.4) * mm, "end": v(-0.08, -6.43) * mm});
            skLineSegment(sketch, "E268", {"start": v(-0.08, -6.43) * mm, "end": v(-0.42, -6.4) * mm});
            skLineSegment(sketch, "E269", {"start": v(-0.42, -6.4) * mm, "end": v(-0.62, -6.38) * mm});
            skLineSegment(sketch, "E270", {"start": v(-0.62, -6.38) * mm, "end": v(-1.06, -6.22) * mm});
            skLineSegment(sketch, "E271", {"start": v(-1.06, -6.22) * mm, "end": v(-1.47, -6) * mm});
            skLineSegment(sketch, "E272", {"start": v(-1.47, -6) * mm, "end": v(-1.82, -5.76) * mm});
            skLineSegment(sketch, "E273", {"start": v(-1.82, -5.76) * mm, "end": v(-2, -5.58) * mm});
            skLineSegment(sketch, "E274", {"start": v(-2, -5.58) * mm, "end": v(-2.13, -5.41) * mm});
            skLineSegment(sketch, "E275", {"start": v(-2.13, -5.41) * mm, "end": v(-2.21, -5.17) * mm});
            skLineSegment(sketch, "E276", {"start": v(-2.21, -5.17) * mm, "end": v(-2.18, -5.02) * mm});
            skLineSegment(sketch, "E277", {"start": v(-2.18, -5.02) * mm, "end": v(-2.07, -4.88) * mm});
            skLineSegment(sketch, "E278", {"start": v(-2.07, -4.88) * mm, "end": v(-1.93, -4.78) * mm});
            skLineSegment(sketch, "E279", {"start": v(-1.93, -4.78) * mm, "end": v(-1.74, -4.67) * mm});
            skLineSegment(sketch, "E280", {"start": v(-1.74, -4.67) * mm, "end": v(-1.3, -4.5) * mm});
            skLineSegment(sketch, "E281", {"start": v(-1.3, -4.5) * mm, "end": v(-0.8, -4.39) * mm});
            skLineSegment(sketch, "E282", {"start": v(-0.8, -4.39) * mm, "end": v(0.09, -4.32) * mm});
            skLineSegment(sketch, "E283", {"start": v(0.09, -4.32) * mm, "end": v(0.83, -4.37) * mm});
            skLineSegment(sketch, "E284", {"start": v(0.83, -4.37) * mm, "end": v(1.46, -4.52) * mm});
            skLineSegment(sketch, "E285", {"start": v(1.46, -4.52) * mm, "end": v(1.71, -4.62) * mm});
            skLineSegment(sketch, "E286", {"start": v(1.71, -4.62) * mm, "end": v(1.91, -4.74) * mm});
            skLineSegment(sketch, "E287", {"start": v(1.91, -4.74) * mm, "end": v(2.05, -4.87) * mm});
            skLineSegment(sketch, "E288", {"start": v(2.05, -4.87) * mm, "end": v(2.12, -5) * mm});
            skLineSegment(sketch, "E289", {"start": v(2.12, -5) * mm, "end": v(2.12, -5.12) * mm});
            skLineSegment(sketch, "E290", {"start": v(2.12, -5.12) * mm, "end": v(2.07, -5.26) * mm});
            skLineSegment(sketch, "E291", {"start": v(2.07, -5.26) * mm, "end": v(1.9, -5.5) * mm});
            skLineSegment(sketch, "E292", {"start": v(1.9, -5.5) * mm, "end": v(1.7, -5.73) * mm});
            skLineSegment(sketch, "E293", {"start": v(1.7, -5.73) * mm, "end": v(1.43, -5.93) * mm});
            skLineSegment(sketch, "E294", {"start": v(5.2, -3.47) * mm, "end": v(4.71, -3.96) * mm});
            skLineSegment(sketch, "E295", {"start": v(4.71, -3.96) * mm, "end": v(4.17, -4.3) * mm});
            skLineSegment(sketch, "E296", {"start": v(4.17, -4.3) * mm, "end": v(3.73, -4.46) * mm});
            skLineSegment(sketch, "E297", {"start": v(3.73, -4.46) * mm, "end": v(3.27, -4.5) * mm});
            skLineSegment(sketch, "E298", {"start": v(3.27, -4.5) * mm, "end": v(3.07, -4.5) * mm});
            skLineSegment(sketch, "E299", {"start": v(3.07, -4.5) * mm, "end": v(2.94, -4.48) * mm});
            skLineSegment(sketch, "E300", {"start": v(2.94, -4.48) * mm, "end": v(2.67, -4.37) * mm});
            skLineSegment(sketch, "E301", {"start": v(2.67, -4.37) * mm, "end": v(2.48, -4.2) * mm});
            skLineSegment(sketch, "E302", {"start": v(2.48, -4.2) * mm, "end": v(2.4, -4) * mm});
            skLineSegment(sketch, "E303", {"start": v(2.4, -4) * mm, "end": v(2.34, -3.75) * mm});
            skLineSegment(sketch, "E304", {"start": v(2.34, -3.75) * mm, "end": v(2.35, -3.42) * mm});
            skLineSegment(sketch, "E305", {"start": v(2.35, -3.42) * mm, "end": v(2.4, -3.05) * mm});
            skLineSegment(sketch, "E306", {"start": v(2.4, -3.05) * mm, "end": v(2.52, -2.66) * mm});
            skLineSegment(sketch, "E307", {"start": v(2.52, -2.66) * mm, "end": v(2.71, -2.2) * mm});
            skLineSegment(sketch, "E308", {"start": v(2.71, -2.2) * mm, "end": v(2.96, -1.77) * mm});
            skLineSegment(sketch, "E309", {"start": v(2.96, -1.77) * mm, "end": v(3.28, -1.38) * mm});
            skLineSegment(sketch, "E310", {"start": v(3.28, -1.38) * mm, "end": v(3.7, -0.98) * mm});
            skLineSegment(sketch, "E311", {"start": v(3.7, -0.98) * mm, "end": v(4.03, -0.71) * mm});
            skLineSegment(sketch, "E312", {"start": v(4.03, -0.71) * mm, "end": v(4.34, -0.52) * mm});
            skLineSegment(sketch, "E313", {"start": v(4.34, -0.52) * mm, "end": v(4.73, -0.39) * mm});
            skLineSegment(sketch, "E314", {"start": v(4.73, -0.39) * mm, "end": v(5.08, -0.4) * mm});
            skLineSegment(sketch, "E315", {"start": v(5.08, -0.4) * mm, "end": v(5.3, -0.5) * mm});
            skLineSegment(sketch, "E316", {"start": v(5.3, -0.5) * mm, "end": v(5.48, -0.68) * mm});
            skLineSegment(sketch, "E317", {"start": v(5.48, -0.68) * mm, "end": v(5.62, -0.98) * mm});
            skLineSegment(sketch, "E318", {"start": v(5.62, -0.98) * mm, "end": v(5.72, -1.35) * mm});
            skLineSegment(sketch, "E319", {"start": v(5.72, -1.35) * mm, "end": v(5.75, -1.76) * mm});
            skLineSegment(sketch, "E320", {"start": v(5.75, -1.76) * mm, "end": v(5.73, -2.26) * mm});
            skLineSegment(sketch, "E321", {"start": v(5.73, -2.26) * mm, "end": v(5.62, -2.72) * mm});
            skLineSegment(sketch, "E322", {"start": v(5.62, -2.72) * mm, "end": v(5.54, -2.94) * mm});
            skLineSegment(sketch, "E323", {"start": v(5.54, -2.94) * mm, "end": v(5.45, -3.12) * mm});
            skLineSegment(sketch, "E324", {"start": v(5.45, -3.12) * mm, "end": v(5.34, -3.28) * mm});
            skLineSegment(sketch, "E325", {"start": v(5.34, -3.28) * mm, "end": v(5.2, -3.47) * mm});
            skLineSegment(sketch, "E326", {"start": v(-2.57, -3.8) * mm, "end": v(-2.68, -4.13) * mm});
            skLineSegment(sketch, "E327", {"start": v(-2.68, -4.13) * mm, "end": v(-2.88, -4.34) * mm});
            skLineSegment(sketch, "E328", {"start": v(-2.88, -4.34) * mm, "end": v(-3.12, -4.42) * mm});
            skLineSegment(sketch, "E329", {"start": v(-3.12, -4.42) * mm, "end": v(-3.45, -4.45) * mm});
            skLineSegment(sketch, "E330", {"start": v(-3.45, -4.45) * mm, "end": v(-3.76, -4.42) * mm});
            skLineSegment(sketch, "E331", {"start": v(-3.76, -4.42) * mm, "end": v(-3.96, -4.38) * mm});
            skLineSegment(sketch, "E332", {"start": v(-3.96, -4.38) * mm, "end": v(-4.48, -4.16) * mm});
            skLineSegment(sketch, "E333", {"start": v(-4.48, -4.16) * mm, "end": v(-4.97, -3.8) * mm});
            skLineSegment(sketch, "E334", {"start": v(-4.97, -3.8) * mm, "end": v(-5.29, -3.47) * mm});
            skLineSegment(sketch, "E335", {"start": v(-5.29, -3.47) * mm, "end": v(-5.53, -3.1) * mm});
            skLineSegment(sketch, "E336", {"start": v(-5.53, -3.1) * mm, "end": v(-5.7, -2.68) * mm});
            skLineSegment(sketch, "E337", {"start": v(-5.7, -2.68) * mm, "end": v(-5.82, -2.22) * mm});
            skLineSegment(sketch, "E338", {"start": v(-5.82, -2.22) * mm, "end": v(-5.87, -1.88) * mm});
            skLineSegment(sketch, "E339", {"start": v(-5.87, -1.88) * mm, "end": v(-5.87, -1.58) * mm});
            skLineSegment(sketch, "E340", {"start": v(-5.87, -1.58) * mm, "end": v(-5.79, -1.21) * mm});
            skLineSegment(sketch, "E341", {"start": v(-5.79, -1.21) * mm, "end": v(-5.65, -0.94) * mm});
            skLineSegment(sketch, "E342", {"start": v(-5.65, -0.94) * mm, "end": v(-5.44, -0.76) * mm});
            skLineSegment(sketch, "E343", {"start": v(-5.44, -0.76) * mm, "end": v(-5.11, -0.68) * mm});
            skLineSegment(sketch, "E344", {"start": v(-5.11, -0.68) * mm, "end": v(-4.7, -0.73) * mm});
            skLineSegment(sketch, "E345", {"start": v(-4.7, -0.73) * mm, "end": v(-4.36, -0.87) * mm});
            skLineSegment(sketch, "E346", {"start": v(-4.36, -0.87) * mm, "end": v(-4, -1.09) * mm});
            skLineSegment(sketch, "E347", {"start": v(-4, -1.09) * mm, "end": v(-3.63, -1.37) * mm});
            skLineSegment(sketch, "E348", {"start": v(-3.63, -1.37) * mm, "end": v(-3.25, -1.75) * mm});
            skLineSegment(sketch, "E349", {"start": v(-3.25, -1.75) * mm, "end": v(-2.96, -2.16) * mm});
            skLineSegment(sketch, "E350", {"start": v(-2.96, -2.16) * mm, "end": v(-2.74, -2.63) * mm});
            skLineSegment(sketch, "E351", {"start": v(-2.74, -2.63) * mm, "end": v(-2.6, -3.12) * mm});
            skLineSegment(sketch, "E352", {"start": v(-2.6, -3.12) * mm, "end": v(-2.56, -3.49) * mm});
            skLineSegment(sketch, "E353", {"start": v(-2.56, -3.49) * mm, "end": v(-2.57, -3.8) * mm});
            skLineSegment(sketch, "E354", {"start": v(2.19, -2.15) * mm, "end": v(2.02, -2.56) * mm});
            skLineSegment(sketch, "E355", {"start": v(2.02, -2.56) * mm, "end": v(1.77, -2.93) * mm});
            skLineSegment(sketch, "E356", {"start": v(1.77, -2.93) * mm, "end": v(1.44, -3.25) * mm});
            skLineSegment(sketch, "E357", {"start": v(1.44, -3.25) * mm, "end": v(0.98, -3.53) * mm});
            skLineSegment(sketch, "E358", {"start": v(0.98, -3.53) * mm, "end": v(0.47, -3.7) * mm});
            skLineSegment(sketch, "E359", {"start": v(0.47, -3.7) * mm, "end": v(0.21, -3.73) * mm});
            skLineSegment(sketch, "E360", {"start": v(0.21, -3.73) * mm, "end": v(-0.1, -3.73) * mm});
            skLineSegment(sketch, "E361", {"start": v(-0.1, -3.73) * mm, "end": v(-0.32, -3.71) * mm});
            skLineSegment(sketch, "E362", {"start": v(-0.32, -3.71) * mm, "end": v(-0.5, -3.69) * mm});
            skLineSegment(sketch, "E363", {"start": v(-0.5, -3.69) * mm, "end": v(-1.09, -3.47) * mm});
            skLineSegment(sketch, "E364", {"start": v(-1.09, -3.47) * mm, "end": v(-1.58, -3.12) * mm});
            skLineSegment(sketch, "E365", {"start": v(-1.58, -3.12) * mm, "end": v(-1.89, -2.76) * mm});
            skLineSegment(sketch, "E366", {"start": v(-1.89, -2.76) * mm, "end": v(-2.1, -2.34) * mm});
            skLineSegment(sketch, "E367", {"start": v(-2.1, -2.34) * mm, "end": v(-2.17, -2.07) * mm});
            skLineSegment(sketch, "E368", {"start": v(-2.17, -2.07) * mm, "end": v(-2.2, -1.74) * mm});
            skLineSegment(sketch, "E369", {"start": v(-2.2, -1.74) * mm, "end": v(-2.2, -1.48) * mm});
            skLineSegment(sketch, "E370", {"start": v(-2.2, -1.48) * mm, "end": v(-2.18, -1.26) * mm});
            skLineSegment(sketch, "E371", {"start": v(-2.18, -1.26) * mm, "end": v(-2.05, -0.88) * mm});
            skLineSegment(sketch, "E372", {"start": v(-2.05, -0.88) * mm, "end": v(-1.84, -0.53) * mm});
            skLineSegment(sketch, "E373", {"start": v(-1.84, -0.53) * mm, "end": v(-1.56, -0.22) * mm});
            skLineSegment(sketch, "E374", {"start": v(-1.56, -0.22) * mm, "end": v(-1.14, 0.08) * mm});
            skLineSegment(sketch, "E375", {"start": v(-1.14, 0.08) * mm, "end": v(-0.67, 0.29) * mm});
            skLineSegment(sketch, "E376", {"start": v(-0.67, 0.29) * mm, "end": v(-0.25, 0.37) * mm});
            skLineSegment(sketch, "E377", {"start": v(-0.25, 0.37) * mm, "end": v(0.2, 0.37) * mm});
            skLineSegment(sketch, "E378", {"start": v(0.2, 0.37) * mm, "end": v(0.55, 0.32) * mm});
            skLineSegment(sketch, "E379", {"start": v(0.55, 0.32) * mm, "end": v(0.88, 0.23) * mm});
            skLineSegment(sketch, "E380", {"start": v(0.88, 0.23) * mm, "end": v(1.37, -0.04) * mm});
            skLineSegment(sketch, "E381", {"start": v(1.37, -0.04) * mm, "end": v(1.78, -0.43) * mm});
            skLineSegment(sketch, "E382", {"start": v(1.78, -0.43) * mm, "end": v(2.03, -0.8) * mm});
            skLineSegment(sketch, "E383", {"start": v(2.03, -0.8) * mm, "end": v(2.18, -1.2) * mm});
            skLineSegment(sketch, "E384", {"start": v(2.18, -1.2) * mm, "end": v(2.22, -1.44) * mm});
            skLineSegment(sketch, "E385", {"start": v(2.22, -1.44) * mm, "end": v(2.23, -1.74) * mm});
            skLineSegment(sketch, "E386", {"start": v(2.23, -1.74) * mm, "end": v(2.22, -1.96) * mm});
            skLineSegment(sketch, "E387", {"start": v(2.22, -1.96) * mm, "end": v(2.19, -2.15) * mm});
            skLineSegment(sketch, "E388", {"start": v(-5.39, 1.02) * mm, "end": v(-5.52, 0.43) * mm});
            skLineSegment(sketch, "E389", {"start": v(-5.52, 0.43) * mm, "end": v(-5.7, -0.06) * mm});
            skLineSegment(sketch, "E390", {"start": v(-5.7, -0.06) * mm, "end": v(-5.84, -0.36) * mm});
            skLineSegment(sketch, "E391", {"start": v(-5.84, -0.36) * mm, "end": v(-5.98, -0.54) * mm});
            skLineSegment(sketch, "E392", {"start": v(-5.98, -0.54) * mm, "end": v(-6.2, -0.62) * mm});
            skLineSegment(sketch, "E393", {"start": v(-6.2, -0.62) * mm, "end": v(-6.38, -0.55) * mm});
            skLineSegment(sketch, "E394", {"start": v(-6.38, -0.55) * mm, "end": v(-6.48, -0.44) * mm});
            skLineSegment(sketch, "E395", {"start": v(-6.48, -0.44) * mm, "end": v(-6.6, -0.28) * mm});
            skLineSegment(sketch, "E396", {"start": v(-6.6, -0.28) * mm, "end": v(-6.78, 0.02) * mm});
            skLineSegment(sketch, "E397", {"start": v(-6.78, 0.02) * mm, "end": v(-6.94, 0.44) * mm});
            skLineSegment(sketch, "E398", {"start": v(-6.94, 0.44) * mm, "end": v(-7.02, 0.88) * mm});
            skLineSegment(sketch, "E399", {"start": v(-7.02, 0.88) * mm, "end": v(-7.02, 1.34) * mm});
            skLineSegment(sketch, "E400", {"start": v(-7.02, 1.34) * mm, "end": v(-6.92, 1.86) * mm});
            skLineSegment(sketch, "E401", {"start": v(-6.92, 1.86) * mm, "end": v(-6.72, 2.33) * mm});
            skLineSegment(sketch, "E402", {"start": v(-6.72, 2.33) * mm, "end": v(-6.46, 2.67) * mm});
            skLineSegment(sketch, "E403", {"start": v(-6.46, 2.67) * mm, "end": v(-6.15, 2.96) * mm});
            skLineSegment(sketch, "E404", {"start": v(-6.15, 2.96) * mm, "end": v(-5.9, 3.13) * mm});
            skLineSegment(sketch, "E405", {"start": v(-5.9, 3.13) * mm, "end": v(-5.73, 3.18) * mm});
            skLineSegment(sketch, "E406", {"start": v(-5.73, 3.18) * mm, "end": v(-5.6, 3.15) * mm});
            skLineSegment(sketch, "E407", {"start": v(-5.6, 3.15) * mm, "end": v(-5.5, 3.05) * mm});
            skLineSegment(sketch, "E408", {"start": v(-5.5, 3.05) * mm, "end": v(-5.37, 2.8) * mm});
            skLineSegment(sketch, "E409", {"start": v(-5.37, 2.8) * mm, "end": v(-5.33, 2.62) * mm});
            skLineSegment(sketch, "E410", {"start": v(-5.33, 2.62) * mm, "end": v(-5.31, 2.36) * mm});
            skLineSegment(sketch, "E411", {"start": v(-5.31, 2.36) * mm, "end": v(-5.31, 1.87) * mm});
            skLineSegment(sketch, "E412", {"start": v(-5.31, 1.87) * mm, "end": v(-5.34, 1.42) * mm});
            skLineSegment(sketch, "E413", {"start": v(-5.34, 1.42) * mm, "end": v(-5.39, 1.02) * mm});
            skLineSegment(sketch, "E414", {"start": v(6.51, 0.07) * mm, "end": v(6.36, -0.19) * mm});
            skLineSegment(sketch, "E415", {"start": v(6.36, -0.19) * mm, "end": v(6.18, -0.41) * mm});
            skLineSegment(sketch, "E416", {"start": v(6.18, -0.41) * mm, "end": v(6.03, -0.55) * mm});
            skLineSegment(sketch, "E417", {"start": v(6.03, -0.55) * mm, "end": v(5.95, -0.59) * mm});
            skLineSegment(sketch, "E418", {"start": v(5.95, -0.59) * mm, "end": v(5.86, -0.56) * mm});
            skLineSegment(sketch, "E419", {"start": v(5.86, -0.56) * mm, "end": v(5.78, -0.52) * mm});
            skLineSegment(sketch, "E420", {"start": v(5.78, -0.52) * mm, "end": v(5.66, -0.42) * mm});
            skLineSegment(sketch, "E421", {"start": v(5.66, -0.42) * mm, "end": v(5.54, -0.25) * mm});
            skLineSegment(sketch, "E422", {"start": v(5.54, -0.25) * mm, "end": v(5.37, 0.13) * mm});
            skLineSegment(sketch, "E423", {"start": v(5.37, 0.13) * mm, "end": v(5.23, 0.57) * mm});
            skLineSegment(sketch, "E424", {"start": v(5.23, 0.57) * mm, "end": v(5.12, 1.1) * mm});
            skLineSegment(sketch, "E425", {"start": v(5.12, 1.1) * mm, "end": v(5.07, 1.43) * mm});
            skLineSegment(sketch, "E426", {"start": v(5.07, 1.43) * mm, "end": v(5.05, 1.8) * mm});
            skLineSegment(sketch, "E427", {"start": v(5.05, 1.8) * mm, "end": v(5.04, 2.18) * mm});
            skLineSegment(sketch, "E428", {"start": v(5.04, 2.18) * mm, "end": v(5.06, 2.57) * mm});
            skLineSegment(sketch, "E429", {"start": v(5.06, 2.57) * mm, "end": v(5.1, 2.84) * mm});
            skLineSegment(sketch, "E430", {"start": v(5.1, 2.84) * mm, "end": v(5.18, 3.02) * mm});
            skLineSegment(sketch, "E431", {"start": v(5.18, 3.02) * mm, "end": v(5.28, 3.15) * mm});
            skLineSegment(sketch, "E432", {"start": v(5.28, 3.15) * mm, "end": v(5.38, 3.22) * mm});
            skLineSegment(sketch, "E433", {"start": v(5.38, 3.22) * mm, "end": v(5.47, 3.24) * mm});
            skLineSegment(sketch, "E434", {"start": v(5.47, 3.24) * mm, "end": v(5.62, 3.2) * mm});
            skLineSegment(sketch, "E435", {"start": v(5.62, 3.2) * mm, "end": v(5.77, 3.1) * mm});
            skLineSegment(sketch, "E436", {"start": v(5.77, 3.1) * mm, "end": v(6.08, 2.86) * mm});
            skLineSegment(sketch, "E437", {"start": v(6.08, 2.86) * mm, "end": v(6.42, 2.43) * mm});
            skLineSegment(sketch, "E438", {"start": v(6.42, 2.43) * mm, "end": v(6.65, 1.93) * mm});
            skLineSegment(sketch, "E439", {"start": v(6.65, 1.93) * mm, "end": v(6.76, 1.39) * mm});
            skLineSegment(sketch, "E440", {"start": v(6.76, 1.39) * mm, "end": v(6.73, 0.72) * mm});
            skLineSegment(sketch, "E441", {"start": v(6.73, 0.72) * mm, "end": v(6.51, 0.07) * mm});
            skLineSegment(sketch, "E442", {"start": v(-0.52, 1.82) * mm, "end": v(-0.7, 1.35) * mm});
            skLineSegment(sketch, "E443", {"start": v(-0.7, 1.35) * mm, "end": v(-0.98, 0.93) * mm});
            skLineSegment(sketch, "E444", {"start": v(-0.98, 0.93) * mm, "end": v(-1.31, 0.56) * mm});
            skLineSegment(sketch, "E445", {"start": v(-1.31, 0.56) * mm, "end": v(-1.79, 0.22) * mm});
            skLineSegment(sketch, "E446", {"start": v(-1.79, 0.22) * mm, "end": v(-2.31, 0) * mm});
            skLineSegment(sketch, "E447", {"start": v(-2.31, 0) * mm, "end": v(-2.6, -0.05) * mm});
            skLineSegment(sketch, "E448", {"start": v(-2.6, -0.05) * mm, "end": v(-2.92, -0.06) * mm});
            skLineSegment(sketch, "E449", {"start": v(-2.92, -0.06) * mm, "end": v(-3.16, -0.05) * mm});
            skLineSegment(sketch, "E450", {"start": v(-3.16, -0.05) * mm, "end": v(-3.36, -0.02) * mm});
            skLineSegment(sketch, "E451", {"start": v(-3.36, -0.02) * mm, "end": v(-3.86, 0.22) * mm});
            skLineSegment(sketch, "E452", {"start": v(-3.86, 0.22) * mm, "end": v(-4.27, 0.6) * mm});
            skLineSegment(sketch, "E453", {"start": v(-4.27, 0.6) * mm, "end": v(-4.5, 0.98) * mm});
            skLineSegment(sketch, "E454", {"start": v(-4.5, 0.98) * mm, "end": v(-4.63, 1.41) * mm});
            skLineSegment(sketch, "E455", {"start": v(-4.63, 1.41) * mm, "end": v(-4.67, 1.77) * mm});
            skLineSegment(sketch, "E456", {"start": v(-4.67, 1.77) * mm, "end": v(-4.66, 2.1) * mm});
            skLineSegment(sketch, "E457", {"start": v(-4.66, 2.1) * mm, "end": v(-4.53, 2.66) * mm});
            skLineSegment(sketch, "E458", {"start": v(-4.53, 2.66) * mm, "end": v(-4.35, 3.07) * mm});
            skLineSegment(sketch, "E459", {"start": v(-4.35, 3.07) * mm, "end": v(-4.09, 3.47) * mm});
            skLineSegment(sketch, "E460", {"start": v(-4.09, 3.47) * mm, "end": v(-3.84, 3.74) * mm});
            skLineSegment(sketch, "E461", {"start": v(-3.84, 3.74) * mm, "end": v(-3.58, 3.97) * mm});
            skLineSegment(sketch, "E462", {"start": v(-3.58, 3.97) * mm, "end": v(-3.37, 4.1) * mm});
            skLineSegment(sketch, "E463", {"start": v(-3.37, 4.1) * mm, "end": v(-3.13, 4.23) * mm});
            skLineSegment(sketch, "E464", {"start": v(-3.13, 4.23) * mm, "end": v(-2.76, 4.37) * mm});
            skLineSegment(sketch, "E465", {"start": v(-2.76, 4.37) * mm, "end": v(-2.45, 4.42) * mm});
            skLineSegment(sketch, "E466", {"start": v(-2.45, 4.42) * mm, "end": v(-2.12, 4.42) * mm});
            skLineSegment(sketch, "E467", {"start": v(-2.12, 4.42) * mm, "end": v(-1.86, 4.4) * mm});
            skLineSegment(sketch, "E468", {"start": v(-1.86, 4.4) * mm, "end": v(-1.64, 4.34) * mm});
            skLineSegment(sketch, "E469", {"start": v(-1.64, 4.34) * mm, "end": v(-1.18, 4.1) * mm});
            skLineSegment(sketch, "E470", {"start": v(-1.18, 4.1) * mm, "end": v(-0.81, 3.74) * mm});
            skLineSegment(sketch, "E471", {"start": v(-0.81, 3.74) * mm, "end": v(-0.6, 3.39) * mm});
            skLineSegment(sketch, "E472", {"start": v(-0.6, 3.39) * mm, "end": v(-0.47, 2.98) * mm});
            skLineSegment(sketch, "E473", {"start": v(-0.47, 2.98) * mm, "end": v(-0.44, 2.68) * mm});
            skLineSegment(sketch, "E474", {"start": v(-0.44, 2.68) * mm, "end": v(-0.44, 2.33) * mm});
            skLineSegment(sketch, "E475", {"start": v(-0.44, 2.33) * mm, "end": v(-0.47, 2.06) * mm});
            skLineSegment(sketch, "E476", {"start": v(-0.47, 2.06) * mm, "end": v(-0.52, 1.82) * mm});
            skLineSegment(sketch, "E477", {"start": v(4.6, 2.07) * mm, "end": v(4.57, 1.57) * mm});
            skLineSegment(sketch, "E478", {"start": v(4.57, 1.57) * mm, "end": v(4.45, 1.13) * mm});
            skLineSegment(sketch, "E479", {"start": v(4.45, 1.13) * mm, "end": v(4.29, 0.83) * mm});
            skLineSegment(sketch, "E480", {"start": v(4.29, 0.83) * mm, "end": v(4.06, 0.55) * mm});
            skLineSegment(sketch, "E481", {"start": v(4.06, 0.55) * mm, "end": v(3.65, 0.24) * mm});
            skLineSegment(sketch, "E482", {"start": v(3.65, 0.24) * mm, "end": v(3.17, 0.07) * mm});
            skLineSegment(sketch, "E483", {"start": v(3.17, 0.07) * mm, "end": v(2.76, 0.03) * mm});
            skLineSegment(sketch, "E484", {"start": v(2.76, 0.03) * mm, "end": v(2.33, 0.08) * mm});
            skLineSegment(sketch, "E485", {"start": v(2.33, 0.08) * mm, "end": v(1.87, 0.25) * mm});
            skLineSegment(sketch, "E486", {"start": v(1.87, 0.25) * mm, "end": v(1.43, 0.52) * mm});
            skLineSegment(sketch, "E487", {"start": v(1.43, 0.52) * mm, "end": v(1.05, 0.88) * mm});
            skLineSegment(sketch, "E488", {"start": v(1.05, 0.88) * mm, "end": v(0.68, 1.4) * mm});
            skLineSegment(sketch, "E489", {"start": v(0.68, 1.4) * mm, "end": v(0.44, 1.98) * mm});
            skLineSegment(sketch, "E490", {"start": v(0.44, 1.98) * mm, "end": v(0.38, 2.35) * mm});
            skLineSegment(sketch, "E491", {"start": v(0.38, 2.35) * mm, "end": v(0.37, 2.74) * mm});
            skLineSegment(sketch, "E492", {"start": v(0.37, 2.74) * mm, "end": v(0.4, 3.03) * mm});
            skLineSegment(sketch, "E493", {"start": v(0.4, 3.03) * mm, "end": v(0.46, 3.3) * mm});
            skLineSegment(sketch, "E494", {"start": v(0.46, 3.3) * mm, "end": v(0.66, 3.73) * mm});
            skLineSegment(sketch, "E495", {"start": v(0.66, 3.73) * mm, "end": v(0.95, 4.08) * mm});
            skLineSegment(sketch, "E496", {"start": v(0.95, 4.08) * mm, "end": v(1.3, 4.33) * mm});
            skLineSegment(sketch, "E497", {"start": v(1.3, 4.33) * mm, "end": v(1.71, 4.49) * mm});
            skLineSegment(sketch, "E498", {"start": v(1.71, 4.49) * mm, "end": v(2.18, 4.54) * mm});
            skLineSegment(sketch, "E499", {"start": v(2.18, 4.54) * mm, "end": v(2.68, 4.47) * mm});
            skLineSegment(sketch, "E500", {"start": v(2.68, 4.47) * mm, "end": v(3.18, 4.28) * mm});
            skLineSegment(sketch, "E501", {"start": v(3.18, 4.28) * mm, "end": v(3.57, 4.02) * mm});
            skLineSegment(sketch, "E502", {"start": v(3.57, 4.02) * mm, "end": v(3.92, 3.7) * mm});
            skLineSegment(sketch, "E503", {"start": v(3.92, 3.7) * mm, "end": v(4.15, 3.4) * mm});
            skLineSegment(sketch, "E504", {"start": v(4.15, 3.4) * mm, "end": v(4.34, 3.07) * mm});
            skLineSegment(sketch, "E505", {"start": v(4.34, 3.07) * mm, "end": v(4.46, 2.8) * mm});
            skLineSegment(sketch, "E506", {"start": v(4.46, 2.8) * mm, "end": v(4.54, 2.54) * mm});
            skLineSegment(sketch, "E507", {"start": v(4.54, 2.54) * mm, "end": v(4.57, 2.32) * mm});
            skLineSegment(sketch, "E508", {"start": v(4.57, 2.32) * mm, "end": v(4.6, 2.07) * mm});
            skLineSegment(sketch, "E509", {"start": v(5.29, 3.82) * mm, "end": v(5.24, 3.75) * mm});
            skLineSegment(sketch, "E510", {"start": v(5.24, 3.75) * mm, "end": v(5.15, 3.73) * mm});
            skLineSegment(sketch, "E511", {"start": v(5.15, 3.73) * mm, "end": v(5.02, 3.75) * mm});
            skLineSegment(sketch, "E512", {"start": v(5.02, 3.75) * mm, "end": v(4.85, 3.82) * mm});
            skLineSegment(sketch, "E513", {"start": v(4.85, 3.82) * mm, "end": v(4.45, 4.05) * mm});
            skLineSegment(sketch, "E514", {"start": v(4.45, 4.05) * mm, "end": v(3.99, 4.39) * mm});
            skLineSegment(sketch, "E515", {"start": v(3.99, 4.39) * mm, "end": v(3.5, 4.79) * mm});
            skLineSegment(sketch, "E516", {"start": v(3.5, 4.79) * mm, "end": v(3.02, 5.21) * mm});
            skLineSegment(sketch, "E517", {"start": v(3.02, 5.21) * mm, "end": v(2.65, 5.58) * mm});
            skLineSegment(sketch, "E518", {"start": v(2.65, 5.58) * mm, "end": v(2.35, 5.9) * mm});
            skLineSegment(sketch, "E519", {"start": v(2.35, 5.9) * mm, "end": v(2.2, 6.12) * mm});
            skLineSegment(sketch, "E520", {"start": v(2.2, 6.12) * mm, "end": v(2.12, 6.29) * mm});
            skLineSegment(sketch, "E521", {"start": v(2.12, 6.29) * mm, "end": v(2.1, 6.36) * mm});
            skLineSegment(sketch, "E522", {"start": v(2.1, 6.36) * mm, "end": v(2.12, 6.4) * mm});
            skLineSegment(sketch, "E523", {"start": v(2.12, 6.4) * mm, "end": v(2.14, 6.43) * mm});
            skLineSegment(sketch, "E524", {"start": v(2.14, 6.43) * mm, "end": v(2.17, 6.45) * mm});
            skLineSegment(sketch, "E525", {"start": v(2.17, 6.45) * mm, "end": v(2.29, 6.47) * mm});
            skLineSegment(sketch, "E526", {"start": v(2.29, 6.47) * mm, "end": v(2.46, 6.5) * mm});
            skLineSegment(sketch, "E527", {"start": v(2.46, 6.5) * mm, "end": v(2.66, 6.5) * mm});
            skLineSegment(sketch, "E528", {"start": v(2.66, 6.5) * mm, "end": v(3.1, 6.49) * mm});
            skLineSegment(sketch, "E529", {"start": v(3.1, 6.49) * mm, "end": v(3.48, 6.43) * mm});
            skLineSegment(sketch, "E530", {"start": v(3.48, 6.43) * mm, "end": v(3.93, 6.27) * mm});
            skLineSegment(sketch, "E531", {"start": v(3.93, 6.27) * mm, "end": v(4.32, 6.04) * mm});
            skLineSegment(sketch, "E532", {"start": v(4.32, 6.04) * mm, "end": v(4.66, 5.75) * mm});
            skLineSegment(sketch, "E533", {"start": v(4.66, 5.75) * mm, "end": v(4.97, 5.32) * mm});
            skLineSegment(sketch, "E534", {"start": v(4.97, 5.32) * mm, "end": v(5.18, 4.83) * mm});
            skLineSegment(sketch, "E535", {"start": v(5.18, 4.83) * mm, "end": v(5.25, 4.53) * mm});
            skLineSegment(sketch, "E536", {"start": v(5.25, 4.53) * mm, "end": v(5.3, 4.19) * mm});
            skLineSegment(sketch, "E537", {"start": v(5.3, 4.19) * mm, "end": v(5.3, 3.94) * mm});
            skLineSegment(sketch, "E538", {"start": v(5.3, 3.94) * mm, "end": v(5.29, 3.82) * mm});
            skLineSegment(sketch, "E539", {"start": v(-2.45, 6.2) * mm, "end": v(-2.57, 6.05) * mm});
            skLineSegment(sketch, "E540", {"start": v(-2.57, 6.05) * mm, "end": v(-2.76, 5.82) * mm});
            skLineSegment(sketch, "E541", {"start": v(-2.76, 5.82) * mm, "end": v(-3.19, 5.38) * mm});
            skLineSegment(sketch, "E542", {"start": v(-3.19, 5.38) * mm, "end": v(-3.62, 4.98) * mm});
            skLineSegment(sketch, "E543", {"start": v(-3.62, 4.98) * mm, "end": v(-4.01, 4.63) * mm});
            skLineSegment(sketch, "E544", {"start": v(-4.01, 4.63) * mm, "end": v(-4.54, 4.23) * mm});
            skLineSegment(sketch, "E545", {"start": v(-4.54, 4.23) * mm, "end": v(-4.97, 3.96) * mm});
            skLineSegment(sketch, "E546", {"start": v(-4.97, 3.96) * mm, "end": v(-5.22, 3.84) * mm});
            skLineSegment(sketch, "E547", {"start": v(-5.22, 3.84) * mm, "end": v(-5.4, 3.8) * mm});
            skLineSegment(sketch, "E548", {"start": v(-5.4, 3.8) * mm, "end": v(-5.5, 3.81) * mm});
            skLineSegment(sketch, "E549", {"start": v(-5.5, 3.81) * mm, "end": v(-5.56, 3.87) * mm});
            skLineSegment(sketch, "E550", {"start": v(-5.56, 3.87) * mm, "end": v(-5.58, 3.98) * mm});
            skLineSegment(sketch, "E551", {"start": v(-5.58, 3.98) * mm, "end": v(-5.58, 4.11) * mm});
            skLineSegment(sketch, "E552", {"start": v(-5.58, 4.11) * mm, "end": v(-5.55, 4.41) * mm});
            skLineSegment(sketch, "E553", {"start": v(-5.55, 4.41) * mm, "end": v(-5.5, 4.7) * mm});
            skLineSegment(sketch, "E554", {"start": v(-5.5, 4.7) * mm, "end": v(-5.44, 4.93) * mm});
            skLineSegment(sketch, "E555", {"start": v(-5.44, 4.93) * mm, "end": v(-5.32, 5.23) * mm});
            skLineSegment(sketch, "E556", {"start": v(-5.32, 5.23) * mm, "end": v(-5.18, 5.48) * mm});
            skLineSegment(sketch, "E557", {"start": v(-5.18, 5.48) * mm, "end": v(-4.86, 5.86) * mm});
            skLineSegment(sketch, "E558", {"start": v(-4.86, 5.86) * mm, "end": v(-4.7, 6.01) * mm});
            skLineSegment(sketch, "E559", {"start": v(-4.7, 6.01) * mm, "end": v(-4.56, 6.12) * mm});
            skLineSegment(sketch, "E560", {"start": v(-4.56, 6.12) * mm, "end": v(-4.29, 6.27) * mm});
            skLineSegment(sketch, "E561", {"start": v(-4.29, 6.27) * mm, "end": v(-3.97, 6.41) * mm});
            skLineSegment(sketch, "E562", {"start": v(-3.97, 6.41) * mm, "end": v(-3.7, 6.5) * mm});
            skLineSegment(sketch, "E563", {"start": v(-3.7, 6.5) * mm, "end": v(-3.45, 6.53) * mm});
            skLineSegment(sketch, "E564", {"start": v(-3.45, 6.53) * mm, "end": v(-3.14, 6.54) * mm});
            skLineSegment(sketch, "E565", {"start": v(-3.14, 6.54) * mm, "end": v(-2.83, 6.55) * mm});
            skLineSegment(sketch, "E566", {"start": v(-2.83, 6.55) * mm, "end": v(-2.61, 6.54) * mm});
            skLineSegment(sketch, "E567", {"start": v(-2.61, 6.54) * mm, "end": v(-2.5, 6.52) * mm});
            skLineSegment(sketch, "E568", {"start": v(-2.5, 6.52) * mm, "end": v(-2.42, 6.48) * mm});
            skLineSegment(sketch, "E569", {"start": v(-2.42, 6.48) * mm, "end": v(-2.39, 6.4) * mm});
            skLineSegment(sketch, "E570", {"start": v(-2.39, 6.4) * mm, "end": v(-2.45, 6.2) * mm});
            skLineSegment(sketch, "E571", {"start": v(1.9, 5.97) * mm, "end": v(1.97, 5.78) * mm});
            skLineSegment(sketch, "E572", {"start": v(1.97, 5.78) * mm, "end": v(2, 5.58) * mm});
            skLineSegment(sketch, "E573", {"start": v(2, 5.58) * mm, "end": v(1.94, 5.3) * mm});
            skLineSegment(sketch, "E574", {"start": v(1.94, 5.3) * mm, "end": v(1.7, 5.02) * mm});
            skLineSegment(sketch, "E575", {"start": v(1.7, 5.02) * mm, "end": v(1.33, 4.8) * mm});
            skLineSegment(sketch, "E576", {"start": v(1.33, 4.8) * mm, "end": v(0.86, 4.64) * mm});
            skLineSegment(sketch, "E577", {"start": v(0.86, 4.64) * mm, "end": v(0.22, 4.55) * mm});
            skLineSegment(sketch, "E578", {"start": v(0.22, 4.55) * mm, "end": v(-0.5, 4.58) * mm});
            skLineSegment(sketch, "E579", {"start": v(-0.5, 4.58) * mm, "end": v(-0.78, 4.64) * mm});
            skLineSegment(sketch, "E580", {"start": v(-0.78, 4.64) * mm, "end": v(-1.09, 4.73) * mm});
            skLineSegment(sketch, "E581", {"start": v(-1.09, 4.73) * mm, "end": v(-1.32, 4.82) * mm});
            skLineSegment(sketch, "E582", {"start": v(-1.32, 4.82) * mm, "end": v(-1.5, 4.92) * mm});
            skLineSegment(sketch, "E583", {"start": v(-1.5, 4.92) * mm, "end": v(-1.84, 5.2) * mm});
            skLineSegment(sketch, "E584", {"start": v(-1.84, 5.2) * mm, "end": v(-1.94, 5.32) * mm});
            skLineSegment(sketch, "E585", {"start": v(-1.94, 5.32) * mm, "end": v(-2, 5.44) * mm});
            skLineSegment(sketch, "E586", {"start": v(-2, 5.44) * mm, "end": v(-2.05, 5.74) * mm});
            skLineSegment(sketch, "E587", {"start": v(-2.05, 5.74) * mm, "end": v(-1.99, 5.96) * mm});
            skLineSegment(sketch, "E588", {"start": v(-1.99, 5.96) * mm, "end": v(-1.89, 6.1) * mm});
            skLineSegment(sketch, "E589", {"start": v(-1.89, 6.1) * mm, "end": v(-1.73, 6.28) * mm});
            skLineSegment(sketch, "E590", {"start": v(-1.73, 6.28) * mm, "end": v(-1.59, 6.4) * mm});
            skLineSegment(sketch, "E591", {"start": v(-1.59, 6.4) * mm, "end": v(-1.45, 6.51) * mm});
            skLineSegment(sketch, "E592", {"start": v(-1.45, 6.51) * mm, "end": v(-1.22, 6.64) * mm});
            skLineSegment(sketch, "E593", {"start": v(-1.22, 6.64) * mm, "end": v(-0.95, 6.77) * mm});
            skLineSegment(sketch, "E594", {"start": v(-0.95, 6.77) * mm, "end": v(-0.73, 6.84) * mm});
            skLineSegment(sketch, "E595", {"start": v(-0.73, 6.84) * mm, "end": v(-0.53, 6.9) * mm});
            skLineSegment(sketch, "E596", {"start": v(-0.53, 6.9) * mm, "end": v(-0.2, 6.94) * mm});
            skLineSegment(sketch, "E597", {"start": v(-0.2, 6.94) * mm, "end": v(0.13, 6.93) * mm});
            skLineSegment(sketch, "E598", {"start": v(0.13, 6.93) * mm, "end": v(0.4, 6.9) * mm});
            skLineSegment(sketch, "E599", {"start": v(0.4, 6.9) * mm, "end": v(0.63, 6.85) * mm});
            skLineSegment(sketch, "E600", {"start": v(0.63, 6.85) * mm, "end": v(1.08, 6.66) * mm});
            skLineSegment(sketch, "E601", {"start": v(1.08, 6.66) * mm, "end": v(1.48, 6.41) * mm});
            skLineSegment(sketch, "E602", {"start": v(1.48, 6.41) * mm, "end": v(1.72, 6.2) * mm});
            skLineSegment(sketch, "E603", {"start": v(1.72, 6.2) * mm, "end": v(1.9, 5.97) * mm});
            skLineSegment(sketch, "E604", {"start": v(-1.42, 8.74) * mm, "end": v(-2.32, 9.34) * mm});
            skLineSegment(sketch, "E605", {"start": v(-2.32, 9.34) * mm, "end": v(-3.09, 9.77) * mm});
            skLineSegment(sketch, "E606", {"start": v(-3.09, 9.77) * mm, "end": v(-3.76, 10.08) * mm});
            skLineSegment(sketch, "E607", {"start": v(-3.76, 10.08) * mm, "end": v(-4.05, 10.2) * mm});
            skLineSegment(sketch, "E608", {"start": v(-4.05, 10.2) * mm, "end": v(-4.14, 10.23) * mm});
            skLineSegment(sketch, "E609", {"start": v(-4.14, 10.23) * mm, "end": v(-4.17, 10.24) * mm});
            skLineSegment(sketch, "E610", {"start": v(-4.17, 10.24) * mm, "end": v(-4.18, 10.24) * mm});
            skLineSegment(sketch, "E611", {"start": v(-4.18, 10.24) * mm, "end": v(-4.18, 10.24) * mm});
            skLineSegment(sketch, "E612", {"start": v(-4.18, 10.24) * mm, "end": v(-4.15, 10.22) * mm});
            skLineSegment(sketch, "E613", {"start": v(-4.15, 10.22) * mm, "end": v(-3.76, 9.98) * mm});
            skLineSegment(sketch, "E614", {"start": v(-3.76, 9.98) * mm, "end": v(-3.02, 9.53) * mm});
            skLineSegment(sketch, "E615", {"start": v(-3.02, 9.53) * mm, "end": v(-2.31, 9.04) * mm});
            skLineSegment(sketch, "E616", {"start": v(-2.31, 9.04) * mm, "end": v(-1.85, 8.68) * mm});
            skLineSegment(sketch, "E617", {"start": v(-1.85, 8.68) * mm, "end": v(-1.5, 8.36) * mm});
            skLineSegment(sketch, "E618", {"start": v(-1.5, 8.36) * mm, "end": v(-1.36, 8.21) * mm});
            skLineSegment(sketch, "E619", {"start": v(-1.36, 8.21) * mm, "end": v(-1.41, 8.03) * mm});
            skLineSegment(sketch, "E620", {"start": v(-1.41, 8.03) * mm, "end": v(-1.6, 7.68) * mm});
            skLineSegment(sketch, "E621", {"start": v(-1.6, 7.68) * mm, "end": v(-1.9, 7.39) * mm});
            skLineSegment(sketch, "E622", {"start": v(-1.9, 7.39) * mm, "end": v(-2.2, 7.2) * mm});
            skLineSegment(sketch, "E623", {"start": v(-2.2, 7.2) * mm, "end": v(-2.57, 7.06) * mm});
            skLineSegment(sketch, "E624", {"start": v(-2.57, 7.06) * mm, "end": v(-2.93, 6.99) * mm});
            skLineSegment(sketch, "E625", {"start": v(-2.93, 6.99) * mm, "end": v(-3.33, 6.93) * mm});
            skLineSegment(sketch, "E626", {"start": v(-3.33, 6.93) * mm, "end": v(-3.62, 6.92) * mm});
            skLineSegment(sketch, "E627", {"start": v(-3.62, 6.92) * mm, "end": v(-3.78, 6.93) * mm});
            skLineSegment(sketch, "E628", {"start": v(-3.78, 6.93) * mm, "end": v(-3.82, 6.95) * mm});
            skLineSegment(sketch, "E629", {"start": v(-3.82, 6.95) * mm, "end": v(-3.83, 6.97) * mm});
            skLineSegment(sketch, "E630", {"start": v(-3.83, 6.97) * mm, "end": v(-3.82, 7) * mm});
            skLineSegment(sketch, "E631", {"start": v(-3.82, 7) * mm, "end": v(-3.8, 7.02) * mm});
            skLineSegment(sketch, "E632", {"start": v(-3.8, 7.02) * mm, "end": v(-3.73, 7.07) * mm});
            skLineSegment(sketch, "E633", {"start": v(-3.73, 7.07) * mm, "end": v(-3.67, 7.13) * mm});
            skLineSegment(sketch, "E634", {"start": v(-3.67, 7.13) * mm, "end": v(-3.66, 7.15) * mm});
            skLineSegment(sketch, "E635", {"start": v(-3.66, 7.15) * mm, "end": v(-3.67, 7.16) * mm});
            skLineSegment(sketch, "E636", {"start": v(-3.67, 7.16) * mm, "end": v(-3.72, 7.18) * mm});
            skLineSegment(sketch, "E637", {"start": v(-3.72, 7.18) * mm, "end": v(-3.78, 7.2) * mm});
            skLineSegment(sketch, "E638", {"start": v(-3.78, 7.2) * mm, "end": v(-4, 7.22) * mm});
            skLineSegment(sketch, "E639", {"start": v(-4, 7.22) * mm, "end": v(-4.24, 7.25) * mm});
            skLineSegment(sketch, "E640", {"start": v(-4.24, 7.25) * mm, "end": v(-4.42, 7.3) * mm});
            skLineSegment(sketch, "E641", {"start": v(-4.42, 7.3) * mm, "end": v(-4.54, 7.34) * mm});
            skLineSegment(sketch, "E642", {"start": v(-4.54, 7.34) * mm, "end": v(-4.57, 7.37) * mm});
            skLineSegment(sketch, "E643", {"start": v(-4.57, 7.37) * mm, "end": v(-4.58, 7.4) * mm});
            skLineSegment(sketch, "E644", {"start": v(-4.58, 7.4) * mm, "end": v(-4.56, 7.43) * mm});
            skLineSegment(sketch, "E645", {"start": v(-4.56, 7.43) * mm, "end": v(-4.5, 7.46) * mm});
            skLineSegment(sketch, "E646", {"start": v(-4.5, 7.46) * mm, "end": v(-4.44, 7.5) * mm});
            skLineSegment(sketch, "E647", {"start": v(-4.44, 7.5) * mm, "end": v(-4.42, 7.51) * mm});
            skLineSegment(sketch, "E648", {"start": v(-4.42, 7.51) * mm, "end": v(-4.42, 7.52) * mm});
            skLineSegment(sketch, "E649", {"start": v(-4.42, 7.52) * mm, "end": v(-4.42, 7.53) * mm});
            skLineSegment(sketch, "E650", {"start": v(-4.42, 7.53) * mm, "end": v(-4.44, 7.53) * mm});
            skLineSegment(sketch, "E651", {"start": v(-4.44, 7.53) * mm, "end": v(-4.48, 7.55) * mm});
            skLineSegment(sketch, "E652", {"start": v(-4.48, 7.55) * mm, "end": v(-4.62, 7.6) * mm});
            skLineSegment(sketch, "E653", {"start": v(-4.62, 7.6) * mm, "end": v(-4.83, 7.68) * mm});
            skLineSegment(sketch, "E654", {"start": v(-4.83, 7.68) * mm, "end": v(-5.03, 7.76) * mm});
            skLineSegment(sketch, "E655", {"start": v(-5.03, 7.76) * mm, "end": v(-5.17, 7.84) * mm});
            skLineSegment(sketch, "E656", {"start": v(-5.17, 7.84) * mm, "end": v(-5.22, 7.88) * mm});
            skLineSegment(sketch, "E657", {"start": v(-5.22, 7.88) * mm, "end": v(-5.23, 7.9) * mm});
            skLineSegment(sketch, "E658", {"start": v(-5.23, 7.9) * mm, "end": v(-5.22, 7.92) * mm});
            skLineSegment(sketch, "E659", {"start": v(-5.22, 7.92) * mm, "end": v(-5.2, 7.94) * mm});
            skLineSegment(sketch, "E660", {"start": v(-5.2, 7.94) * mm, "end": v(-5.1, 7.97) * mm});
            skLineSegment(sketch, "E661", {"start": v(-5.1, 7.97) * mm, "end": v(-4.95, 8) * mm});
            skLineSegment(sketch, "E662", {"start": v(-4.95, 8) * mm, "end": v(-5.21, 8.14) * mm});
            skLineSegment(sketch, "E663", {"start": v(-5.21, 8.14) * mm, "end": v(-5.6, 8.39) * mm});
            skLineSegment(sketch, "E664", {"start": v(-5.6, 8.39) * mm, "end": v(-5.7, 8.48) * mm});
            skLineSegment(sketch, "E665", {"start": v(-5.7, 8.48) * mm, "end": v(-5.74, 8.52) * mm});
            skLineSegment(sketch, "E666", {"start": v(-5.74, 8.52) * mm, "end": v(-5.74, 8.55) * mm});
            skLineSegment(sketch, "E667", {"start": v(-5.74, 8.55) * mm, "end": v(-5.73, 8.56) * mm});
            skLineSegment(sketch, "E668", {"start": v(-5.73, 8.56) * mm, "end": v(-5.72, 8.57) * mm});
            skLineSegment(sketch, "E669", {"start": v(-5.72, 8.57) * mm, "end": v(-5.68, 8.58) * mm});
            skLineSegment(sketch, "E670", {"start": v(-5.68, 8.58) * mm, "end": v(-5.59, 8.6) * mm});
            skLineSegment(sketch, "E671", {"start": v(-5.59, 8.6) * mm, "end": v(-5.45, 8.62) * mm});
            skLineSegment(sketch, "E672", {"start": v(-5.45, 8.62) * mm, "end": v(-5.62, 8.74) * mm});
            skLineSegment(sketch, "E673", {"start": v(-5.62, 8.74) * mm, "end": v(-5.8, 8.87) * mm});
            skLineSegment(sketch, "E674", {"start": v(-5.8, 8.87) * mm, "end": v(-5.94, 9) * mm});
            skLineSegment(sketch, "E675", {"start": v(-5.94, 9) * mm, "end": v(-6.04, 9.12) * mm});
            skLineSegment(sketch, "E676", {"start": v(-6.04, 9.12) * mm, "end": v(-6.05, 9.19) * mm});
            skLineSegment(sketch, "E677", {"start": v(-6.05, 9.19) * mm, "end": v(-6.04, 9.2) * mm});
            skLineSegment(sketch, "E678", {"start": v(-6.04, 9.2) * mm, "end": v(-6.03, 9.2) * mm});
            skLineSegment(sketch, "E679", {"start": v(-6.03, 9.2) * mm, "end": v(-5.97, 9.2) * mm});
            skLineSegment(sketch, "E680", {"start": v(-5.97, 9.2) * mm, "end": v(-5.89, 9.2) * mm});
            skLineSegment(sketch, "E681", {"start": v(-5.89, 9.2) * mm, "end": v(-5.83, 9.21) * mm});
            skLineSegment(sketch, "E682", {"start": v(-5.83, 9.21) * mm, "end": v(-5.8, 9.23) * mm});
            skLineSegment(sketch, "E683", {"start": v(-5.8, 9.23) * mm, "end": v(-5.81, 9.25) * mm});
            skLineSegment(sketch, "E684", {"start": v(-5.81, 9.25) * mm, "end": v(-5.83, 9.28) * mm});
            skLineSegment(sketch, "E685", {"start": v(-5.83, 9.28) * mm, "end": v(-5.95, 9.39) * mm});
            skLineSegment(sketch, "E686", {"start": v(-5.95, 9.39) * mm, "end": v(-6.1, 9.53) * mm});
            skLineSegment(sketch, "E687", {"start": v(-6.1, 9.53) * mm, "end": v(-6.22, 9.67) * mm});
            skLineSegment(sketch, "E688", {"start": v(-6.22, 9.67) * mm, "end": v(-6.28, 9.78) * mm});
            skLineSegment(sketch, "E689", {"start": v(-6.28, 9.78) * mm, "end": v(-6.3, 9.84) * mm});
            skLineSegment(sketch, "E690", {"start": v(-6.3, 9.84) * mm, "end": v(-6.3, 9.86) * mm});
            skLineSegment(sketch, "E691", {"start": v(-6.3, 9.86) * mm, "end": v(-6.26, 9.87) * mm});
            skLineSegment(sketch, "E692", {"start": v(-6.26, 9.87) * mm, "end": v(-6.11, 9.87) * mm});
            skLineSegment(sketch, "E693", {"start": v(-6.11, 9.87) * mm, "end": v(-5.93, 9.86) * mm});
            skLineSegment(sketch, "E694", {"start": v(-5.93, 9.86) * mm, "end": v(-6.11, 10.03) * mm});
            skLineSegment(sketch, "E695", {"start": v(-6.11, 10.03) * mm, "end": v(-6.25, 10.18) * mm});
            skLineSegment(sketch, "E696", {"start": v(-6.25, 10.18) * mm, "end": v(-6.38, 10.33) * mm});
            skLineSegment(sketch, "E697", {"start": v(-6.38, 10.33) * mm, "end": v(-6.44, 10.43) * mm});
            skLineSegment(sketch, "E698", {"start": v(-6.44, 10.43) * mm, "end": v(-6.46, 10.49) * mm});
            skLineSegment(sketch, "E699", {"start": v(-6.46, 10.49) * mm, "end": v(-6.46, 10.5) * mm});
            skLineSegment(sketch, "E700", {"start": v(-6.46, 10.5) * mm, "end": v(-6.45, 10.5) * mm});
            skLineSegment(sketch, "E701", {"start": v(-6.45, 10.5) * mm, "end": v(-6.41, 10.5) * mm});
            skLineSegment(sketch, "E702", {"start": v(-6.41, 10.5) * mm, "end": v(-6.29, 10.51) * mm});
            skLineSegment(sketch, "E703", {"start": v(-6.29, 10.51) * mm, "end": v(-6.15, 10.52) * mm});
            skLineSegment(sketch, "E704", {"start": v(-6.15, 10.52) * mm, "end": v(-6.12, 10.54) * mm});
            skLineSegment(sketch, "E705", {"start": v(-6.12, 10.54) * mm, "end": v(-6.1, 10.55) * mm});
            skLineSegment(sketch, "E706", {"start": v(-6.1, 10.55) * mm, "end": v(-6.12, 10.6) * mm});
            skLineSegment(sketch, "E707", {"start": v(-6.12, 10.6) * mm, "end": v(-6.14, 10.67) * mm});
            skLineSegment(sketch, "E708", {"start": v(-6.14, 10.67) * mm, "end": v(-6.2, 10.8) * mm});
            skLineSegment(sketch, "E709", {"start": v(-6.2, 10.8) * mm, "end": v(-6.27, 10.94) * mm});
            skLineSegment(sketch, "E710", {"start": v(-6.27, 10.94) * mm, "end": v(-6.33, 11.03) * mm});
            skLineSegment(sketch, "E711", {"start": v(-6.33, 11.03) * mm, "end": v(-6.4, 11.14) * mm});
            skLineSegment(sketch, "E712", {"start": v(-6.4, 11.14) * mm, "end": v(-6.4, 11.17) * mm});
            skLineSegment(sketch, "E713", {"start": v(-6.4, 11.17) * mm, "end": v(-6.4, 11.19) * mm});
            skLineSegment(sketch, "E714", {"start": v(-6.4, 11.19) * mm, "end": v(-6.34, 11.21) * mm});
            skLineSegment(sketch, "E715", {"start": v(-6.34, 11.21) * mm, "end": v(-6.25, 11.22) * mm});
            skLineSegment(sketch, "E716", {"start": v(-6.25, 11.22) * mm, "end": v(-5.99, 11.23) * mm});
            skLineSegment(sketch, "E717", {"start": v(-5.99, 11.23) * mm, "end": v(-5.58, 11.23) * mm});
            skLineSegment(sketch, "E718", {"start": v(-5.58, 11.23) * mm, "end": v(-5.67, 11.33) * mm});
            skLineSegment(sketch, "E719", {"start": v(-5.67, 11.33) * mm, "end": v(-5.73, 11.4) * mm});
            skLineSegment(sketch, "E720", {"start": v(-5.73, 11.4) * mm, "end": v(-5.73, 11.44) * mm});
            skLineSegment(sketch, "E721", {"start": v(-5.73, 11.44) * mm, "end": v(-5.68, 11.48) * mm});
            skLineSegment(sketch, "E722", {"start": v(-5.68, 11.48) * mm, "end": v(-5.53, 11.5) * mm});
            skLineSegment(sketch, "E723", {"start": v(-5.53, 11.5) * mm, "end": v(-5.36, 11.5) * mm});
            skLineSegment(sketch, "E724", {"start": v(-5.36, 11.5) * mm, "end": v(-5.11, 11.48) * mm});
            skLineSegment(sketch, "E725", {"start": v(-5.11, 11.48) * mm, "end": v(-4.93, 11.44) * mm});
            skLineSegment(sketch, "E726", {"start": v(-4.93, 11.44) * mm, "end": v(-4.8, 11.4) * mm});
            skLineSegment(sketch, "E727", {"start": v(-4.8, 11.4) * mm, "end": v(-4.75, 11.4) * mm});
            skLineSegment(sketch, "E728", {"start": v(-4.75, 11.4) * mm, "end": v(-4.74, 11.42) * mm});
            skLineSegment(sketch, "E729", {"start": v(-4.74, 11.42) * mm, "end": v(-4.75, 11.46) * mm});
            skLineSegment(sketch, "E730", {"start": v(-4.75, 11.46) * mm, "end": v(-4.82, 11.55) * mm});
            skLineSegment(sketch, "E731", {"start": v(-4.82, 11.55) * mm, "end": v(-4.88, 11.63) * mm});
            skLineSegment(sketch, "E732", {"start": v(-4.88, 11.63) * mm, "end": v(-4.88, 11.68) * mm});
            skLineSegment(sketch, "E733", {"start": v(-4.88, 11.68) * mm, "end": v(-4.81, 11.7) * mm});
            skLineSegment(sketch, "E734", {"start": v(-4.81, 11.7) * mm, "end": v(-4.68, 11.68) * mm});
            skLineSegment(sketch, "E735", {"start": v(-4.68, 11.68) * mm, "end": v(-4.24, 11.57) * mm});
            skLineSegment(sketch, "E736", {"start": v(-4.24, 11.57) * mm, "end": v(-4.11, 11.54) * mm});
            skLineSegment(sketch, "E737", {"start": v(-4.11, 11.54) * mm, "end": v(-4.08, 11.54) * mm});
            skLineSegment(sketch, "E738", {"start": v(-4.08, 11.54) * mm, "end": v(-4.07, 11.54) * mm});
            skLineSegment(sketch, "E739", {"start": v(-4.07, 11.54) * mm, "end": v(-4.07, 11.54) * mm});
            skLineSegment(sketch, "E740", {"start": v(-4.07, 11.54) * mm, "end": v(-4.06, 11.54) * mm});
            skLineSegment(sketch, "E741", {"start": v(-4.06, 11.54) * mm, "end": v(-4.07, 11.55) * mm});
            skLineSegment(sketch, "E742", {"start": v(-4.07, 11.55) * mm, "end": v(-4.09, 11.58) * mm});
            skLineSegment(sketch, "E743", {"start": v(-4.09, 11.58) * mm, "end": v(-4.15, 11.66) * mm});
            skLineSegment(sketch, "E744", {"start": v(-4.15, 11.66) * mm, "end": v(-4.25, 11.78) * mm});
            skLineSegment(sketch, "E745", {"start": v(-4.25, 11.78) * mm, "end": v(-4.26, 11.8) * mm});
            skLineSegment(sketch, "E746", {"start": v(-4.26, 11.8) * mm, "end": v(-4.25, 11.83) * mm});
            skLineSegment(sketch, "E747", {"start": v(-4.25, 11.83) * mm, "end": v(-4.2, 11.84) * mm});
            skLineSegment(sketch, "E748", {"start": v(-4.2, 11.84) * mm, "end": v(-4.14, 11.84) * mm});
            skLineSegment(sketch, "E749", {"start": v(-4.14, 11.84) * mm, "end": v(-3.88, 11.77) * mm});
            skLineSegment(sketch, "E750", {"start": v(-3.88, 11.77) * mm, "end": v(-3.66, 11.68) * mm});
            skLineSegment(sketch, "E751", {"start": v(-3.66, 11.68) * mm, "end": v(-3.54, 11.62) * mm});
            skLineSegment(sketch, "E752", {"start": v(-3.54, 11.62) * mm, "end": v(-3.45, 11.57) * mm});
            skLineSegment(sketch, "E753", {"start": v(-3.45, 11.57) * mm, "end": v(-3.42, 11.56) * mm});
            skLineSegment(sketch, "E754", {"start": v(-3.42, 11.56) * mm, "end": v(-3.4, 11.55) * mm});
            skLineSegment(sketch, "E755", {"start": v(-3.4, 11.55) * mm, "end": v(-3.4, 11.56) * mm});
            skLineSegment(sketch, "E756", {"start": v(-3.4, 11.56) * mm, "end": v(-3.38, 11.57) * mm});
            skLineSegment(sketch, "E757", {"start": v(-3.38, 11.57) * mm, "end": v(-3.38, 11.6) * mm});
            skLineSegment(sketch, "E758", {"start": v(-3.38, 11.6) * mm, "end": v(-3.4, 11.65) * mm});
            skLineSegment(sketch, "E759", {"start": v(-3.4, 11.65) * mm, "end": v(-3.44, 11.74) * mm});
            skLineSegment(sketch, "E760", {"start": v(-3.44, 11.74) * mm, "end": v(-3.47, 11.82) * mm});
            skLineSegment(sketch, "E761", {"start": v(-3.47, 11.82) * mm, "end": v(-3.47, 11.85) * mm});
            skLineSegment(sketch, "E762", {"start": v(-3.47, 11.85) * mm, "end": v(-3.47, 11.86) * mm});
            skLineSegment(sketch, "E763", {"start": v(-3.47, 11.86) * mm, "end": v(-3.45, 11.87) * mm});
            skLineSegment(sketch, "E764", {"start": v(-3.45, 11.87) * mm, "end": v(-3.4, 11.86) * mm});
            skLineSegment(sketch, "E765", {"start": v(-3.4, 11.86) * mm, "end": v(-3.29, 11.81) * mm});
            skLineSegment(sketch, "E766", {"start": v(-3.29, 11.81) * mm, "end": v(-2.97, 11.61) * mm});
            skLineSegment(sketch, "E767", {"start": v(-2.97, 11.61) * mm, "end": v(-2.81, 11.51) * mm});
            skLineSegment(sketch, "E768", {"start": v(-2.81, 11.51) * mm, "end": v(-2.76, 11.5) * mm});
            skLineSegment(sketch, "E769", {"start": v(-2.76, 11.5) * mm, "end": v(-2.73, 11.5) * mm});
            skLineSegment(sketch, "E770", {"start": v(-2.73, 11.5) * mm, "end": v(-2.7, 11.54) * mm});
            skLineSegment(sketch, "E771", {"start": v(-2.7, 11.54) * mm, "end": v(-2.72, 11.66) * mm});
            skLineSegment(sketch, "E772", {"start": v(-2.72, 11.66) * mm, "end": v(-2.72, 11.75) * mm});
            skLineSegment(sketch, "E773", {"start": v(-2.72, 11.75) * mm, "end": v(-2.72, 11.77) * mm});
            skLineSegment(sketch, "E774", {"start": v(-2.72, 11.77) * mm, "end": v(-2.7, 11.78) * mm});
            skLineSegment(sketch, "E775", {"start": v(-2.7, 11.78) * mm, "end": v(-2.68, 11.77) * mm});
            skLineSegment(sketch, "E776", {"start": v(-2.68, 11.77) * mm, "end": v(-2.65, 11.76) * mm});
            skLineSegment(sketch, "E777", {"start": v(-2.65, 11.76) * mm, "end": v(-2.6, 11.73) * mm});
            skLineSegment(sketch, "E778", {"start": v(-2.6, 11.73) * mm, "end": v(-2.47, 11.64) * mm});
            skLineSegment(sketch, "E779", {"start": v(-2.47, 11.64) * mm, "end": v(-2.25, 11.44) * mm});
            skLineSegment(sketch, "E780", {"start": v(-2.25, 11.44) * mm, "end": v(-2.16, 11.37) * mm});
            skLineSegment(sketch, "E781", {"start": v(-2.16, 11.37) * mm, "end": v(-2.13, 11.35) * mm});
            skLineSegment(sketch, "E782", {"start": v(-2.13, 11.35) * mm, "end": v(-2.1, 11.35) * mm});
            skLineSegment(sketch, "E783", {"start": v(-2.1, 11.35) * mm, "end": v(-2.1, 11.35) * mm});
            skLineSegment(sketch, "E784", {"start": v(-2.1, 11.35) * mm, "end": v(-2.1, 11.37) * mm});
            skLineSegment(sketch, "E785", {"start": v(-2.1, 11.37) * mm, "end": v(-2.09, 11.4) * mm});
            skLineSegment(sketch, "E786", {"start": v(-2.09, 11.4) * mm, "end": v(-2.08, 11.49) * mm});
            skLineSegment(sketch, "E787", {"start": v(-2.08, 11.49) * mm, "end": v(-2.07, 11.59) * mm});
            skLineSegment(sketch, "E788", {"start": v(-2.07, 11.59) * mm, "end": v(-2.06, 11.61) * mm});
            skLineSegment(sketch, "E789", {"start": v(-2.06, 11.61) * mm, "end": v(-2.03, 11.62) * mm});
            skLineSegment(sketch, "E790", {"start": v(-2.03, 11.62) * mm, "end": v(-2, 11.6) * mm});
            skLineSegment(sketch, "E791", {"start": v(-2, 11.6) * mm, "end": v(-1.95, 11.57) * mm});
            skLineSegment(sketch, "E792", {"start": v(-1.95, 11.57) * mm, "end": v(-1.84, 11.48) * mm});
            skLineSegment(sketch, "E793", {"start": v(-1.84, 11.48) * mm, "end": v(-1.57, 11.19) * mm});
            skLineSegment(sketch, "E794", {"start": v(-1.57, 11.19) * mm, "end": v(-1.46, 11.07) * mm});
            skLineSegment(sketch, "E795", {"start": v(-1.46, 11.07) * mm, "end": v(-1.43, 11.04) * mm});
            skLineSegment(sketch, "E796", {"start": v(-1.43, 11.04) * mm, "end": v(-1.42, 11.04) * mm});
            skLineSegment(sketch, "E797", {"start": v(-1.42, 11.04) * mm, "end": v(-1.42, 11.03) * mm});
            skLineSegment(sketch, "E798", {"start": v(-1.42, 11.03) * mm, "end": v(-1.42, 11.03) * mm});
            skLineSegment(sketch, "E799", {"start": v(-1.42, 11.03) * mm, "end": v(-1.42, 11.04) * mm});
            skLineSegment(sketch, "E800", {"start": v(-1.42, 11.04) * mm, "end": v(-1.41, 11.04) * mm});
            skLineSegment(sketch, "E801", {"start": v(-1.41, 11.04) * mm, "end": v(-1.4, 11.06) * mm});
            skLineSegment(sketch, "E802", {"start": v(-1.4, 11.06) * mm, "end": v(-1.38, 11.13) * mm});
            skLineSegment(sketch, "E803", {"start": v(-1.38, 11.13) * mm, "end": v(-1.35, 11.21) * mm});
            skLineSegment(sketch, "E804", {"start": v(-1.35, 11.21) * mm, "end": v(-1.33, 11.25) * mm});
            skLineSegment(sketch, "E805", {"start": v(-1.33, 11.25) * mm, "end": v(-1.31, 11.25) * mm});
            skLineSegment(sketch, "E806", {"start": v(-1.31, 11.25) * mm, "end": v(-1.3, 11.24) * mm});
            skLineSegment(sketch, "E807", {"start": v(-1.3, 11.24) * mm, "end": v(-1.24, 11.2) * mm});
            skLineSegment(sketch, "E808", {"start": v(-1.24, 11.2) * mm, "end": v(-1.1, 11.05) * mm});
            skLineSegment(sketch, "E809", {"start": v(-1.1, 11.05) * mm, "end": v(-0.92, 10.84) * mm});
            skLineSegment(sketch, "E810", {"start": v(-0.92, 10.84) * mm, "end": v(-0.77, 10.6) * mm});
            skLineSegment(sketch, "E811", {"start": v(-0.77, 10.6) * mm, "end": v(-0.54, 10.12) * mm});
            skLineSegment(sketch, "E812", {"start": v(-0.54, 10.12) * mm, "end": v(-0.42, 9.67) * mm});
            skLineSegment(sketch, "E813", {"start": v(-0.42, 9.67) * mm, "end": v(-0.42, 9.35) * mm});
            skLineSegment(sketch, "E814", {"start": v(-0.42, 9.35) * mm, "end": v(-0.49, 9.07) * mm});
            skLineSegment(sketch, "E815", {"start": v(-0.49, 9.07) * mm, "end": v(-0.6, 8.9) * mm});
            skLineSegment(sketch, "E816", {"start": v(-0.6, 8.9) * mm, "end": v(-0.74, 8.73) * mm});
            skLineSegment(sketch, "E817", {"start": v(-0.74, 8.73) * mm, "end": v(-0.86, 8.62) * mm});
            skLineSegment(sketch, "E818", {"start": v(-0.86, 8.62) * mm, "end": v(-0.98, 8.55) * mm});
            skLineSegment(sketch, "E819", {"start": v(-0.98, 8.55) * mm, "end": v(-1.1, 8.5) * mm});
            skLineSegment(sketch, "E820", {"start": v(-1.1, 8.5) * mm, "end": v(-1.42, 8.74) * mm});
            skLineSegment(sketch, "E821", {"start": v(4.68, 7.64) * mm, "end": v(4.48, 7.56) * mm});
            skLineSegment(sketch, "E822", {"start": v(4.48, 7.56) * mm, "end": v(4.42, 7.54) * mm});
            skLineSegment(sketch, "E823", {"start": v(4.42, 7.54) * mm, "end": v(4.4, 7.53) * mm});
            skLineSegment(sketch, "E824", {"start": v(4.4, 7.53) * mm, "end": v(4.4, 7.52) * mm});
            skLineSegment(sketch, "E825", {"start": v(4.4, 7.52) * mm, "end": v(4.4, 7.52) * mm});
            skLineSegment(sketch, "E826", {"start": v(4.4, 7.52) * mm, "end": v(4.4, 7.5) * mm});
            skLineSegment(sketch, "E827", {"start": v(4.4, 7.5) * mm, "end": v(4.43, 7.49) * mm});
            skLineSegment(sketch, "E828", {"start": v(4.43, 7.49) * mm, "end": v(4.47, 7.47) * mm});
            skLineSegment(sketch, "E829", {"start": v(4.47, 7.47) * mm, "end": v(4.55, 7.43) * mm});
            skLineSegment(sketch, "E830", {"start": v(4.55, 7.43) * mm, "end": v(4.57, 7.4) * mm});
            skLineSegment(sketch, "E831", {"start": v(4.57, 7.4) * mm, "end": v(4.57, 7.38) * mm});
            skLineSegment(sketch, "E832", {"start": v(4.57, 7.38) * mm, "end": v(4.55, 7.35) * mm});
            skLineSegment(sketch, "E833", {"start": v(4.55, 7.35) * mm, "end": v(4.46, 7.31) * mm});
            skLineSegment(sketch, "E834", {"start": v(4.46, 7.31) * mm, "end": v(4.32, 7.27) * mm});
            skLineSegment(sketch, "E835", {"start": v(4.32, 7.27) * mm, "end": v(4, 7.22) * mm});
            skLineSegment(sketch, "E836", {"start": v(4, 7.22) * mm, "end": v(3.74, 7.18) * mm});
            skLineSegment(sketch, "E837", {"start": v(3.74, 7.18) * mm, "end": v(3.65, 7.15) * mm});
            skLineSegment(sketch, "E838", {"start": v(3.65, 7.15) * mm, "end": v(3.64, 7.13) * mm});
            skLineSegment(sketch, "E839", {"start": v(3.64, 7.13) * mm, "end": v(3.64, 7.12) * mm});
            skLineSegment(sketch, "E840", {"start": v(3.64, 7.12) * mm, "end": v(3.67, 7.1) * mm});
            skLineSegment(sketch, "E841", {"start": v(3.67, 7.1) * mm, "end": v(3.7, 7.07) * mm});
            skLineSegment(sketch, "E842", {"start": v(3.7, 7.07) * mm, "end": v(3.77, 7.03) * mm});
            skLineSegment(sketch, "E843", {"start": v(3.77, 7.03) * mm, "end": v(3.79, 7) * mm});
            skLineSegment(sketch, "E844", {"start": v(3.79, 7) * mm, "end": v(3.8, 7) * mm});
            skLineSegment(sketch, "E845", {"start": v(3.8, 7) * mm, "end": v(3.79, 6.96) * mm});
            skLineSegment(sketch, "E846", {"start": v(3.79, 6.96) * mm, "end": v(3.76, 6.94) * mm});
            skLineSegment(sketch, "E847", {"start": v(3.76, 6.94) * mm, "end": v(3.67, 6.92) * mm});
            skLineSegment(sketch, "E848", {"start": v(3.67, 6.92) * mm, "end": v(3.54, 6.92) * mm});
            skLineSegment(sketch, "E849", {"start": v(3.54, 6.92) * mm, "end": v(3.37, 6.93) * mm});
            skLineSegment(sketch, "E850", {"start": v(3.37, 6.93) * mm, "end": v(3.15, 6.95) * mm});
            skLineSegment(sketch, "E851", {"start": v(3.15, 6.95) * mm, "end": v(2.51, 7.07) * mm});
            skLineSegment(sketch, "E852", {"start": v(2.51, 7.07) * mm, "end": v(1.99, 7.31) * mm});
            skLineSegment(sketch, "E853", {"start": v(1.99, 7.31) * mm, "end": v(1.67, 7.56) * mm});
            skLineSegment(sketch, "E854", {"start": v(1.67, 7.56) * mm, "end": v(1.46, 7.86) * mm});
            skLineSegment(sketch, "E855", {"start": v(1.46, 7.86) * mm, "end": v(1.4, 8) * mm});
            skLineSegment(sketch, "E856", {"start": v(1.4, 8) * mm, "end": v(1.36, 8.1) * mm});
            skLineSegment(sketch, "E857", {"start": v(1.36, 8.1) * mm, "end": v(1.35, 8.2) * mm});
            skLineSegment(sketch, "E858", {"start": v(1.35, 8.2) * mm, "end": v(1.42, 8.3) * mm});
            skLineSegment(sketch, "E859", {"start": v(1.42, 8.3) * mm, "end": v(1.54, 8.42) * mm});
            skLineSegment(sketch, "E860", {"start": v(1.54, 8.42) * mm, "end": v(2.01, 8.83) * mm});
            skLineSegment(sketch, "E861", {"start": v(2.01, 8.83) * mm, "end": v(2.62, 9.28) * mm});
            skLineSegment(sketch, "E862", {"start": v(2.62, 9.28) * mm, "end": v(3.17, 9.65) * mm});
            skLineSegment(sketch, "E863", {"start": v(3.17, 9.65) * mm, "end": v(3.78, 10.01) * mm});
            skLineSegment(sketch, "E864", {"start": v(3.78, 10.01) * mm, "end": v(4.15, 10.24) * mm});
            skLineSegment(sketch, "E865", {"start": v(4.15, 10.24) * mm, "end": v(4.17, 10.25) * mm});
            skLineSegment(sketch, "E866", {"start": v(4.17, 10.25) * mm, "end": v(4.18, 10.25) * mm});
            skLineSegment(sketch, "E867", {"start": v(4.18, 10.25) * mm, "end": v(4.18, 10.26) * mm});
            skLineSegment(sketch, "E868", {"start": v(4.18, 10.26) * mm, "end": v(4.18, 10.26) * mm});
            skLineSegment(sketch, "E869", {"start": v(4.18, 10.26) * mm, "end": v(4.17, 10.26) * mm});
            skLineSegment(sketch, "E870", {"start": v(4.17, 10.26) * mm, "end": v(4.15, 10.25) * mm});
            skLineSegment(sketch, "E871", {"start": v(4.15, 10.25) * mm, "end": v(3.75, 10.09) * mm});
            skLineSegment(sketch, "E872", {"start": v(3.75, 10.09) * mm, "end": v(3.05, 9.76) * mm});
            skLineSegment(sketch, "E873", {"start": v(3.05, 9.76) * mm, "end": v(2.4, 9.4) * mm});
            skLineSegment(sketch, "E874", {"start": v(2.4, 9.4) * mm, "end": v(1.46, 8.79) * mm});
            skLineSegment(sketch, "E875", {"start": v(1.46, 8.79) * mm, "end": v(1.3, 8.66) * mm});
            skLineSegment(sketch, "E876", {"start": v(1.3, 8.66) * mm, "end": v(1.16, 8.57) * mm});
            skLineSegment(sketch, "E877", {"start": v(1.16, 8.57) * mm, "end": v(1.08, 8.52) * mm});
            skLineSegment(sketch, "E878", {"start": v(1.08, 8.52) * mm, "end": v(1.06, 8.5) * mm});
            skLineSegment(sketch, "E879", {"start": v(1.06, 8.5) * mm, "end": v(1.05, 8.5) * mm});
            skLineSegment(sketch, "E880", {"start": v(1.05, 8.5) * mm, "end": v(1.05, 8.5) * mm});
            skLineSegment(sketch, "E881", {"start": v(1.05, 8.5) * mm, "end": v(1, 8.52) * mm});
            skLineSegment(sketch, "E882", {"start": v(1, 8.52) * mm, "end": v(0.94, 8.55) * mm});
            skLineSegment(sketch, "E883", {"start": v(0.94, 8.55) * mm, "end": v(0.82, 8.63) * mm});
            skLineSegment(sketch, "E884", {"start": v(0.82, 8.63) * mm, "end": v(0.7, 8.72) * mm});
            skLineSegment(sketch, "E885", {"start": v(0.7, 8.72) * mm, "end": v(0.63, 8.8) * mm});
            skLineSegment(sketch, "E886", {"start": v(0.63, 8.8) * mm, "end": v(0.5, 8.97) * mm});
            skLineSegment(sketch, "E887", {"start": v(0.5, 8.97) * mm, "end": v(0.43, 9.14) * mm});
            skLineSegment(sketch, "E888", {"start": v(0.43, 9.14) * mm, "end": v(0.4, 9.3) * mm});
            skLineSegment(sketch, "E889", {"start": v(0.4, 9.3) * mm, "end": v(0.4, 9.5) * mm});
            skLineSegment(sketch, "E890", {"start": v(0.4, 9.5) * mm, "end": v(0.4, 9.71) * mm});
            skLineSegment(sketch, "E891", {"start": v(0.4, 9.71) * mm, "end": v(0.42, 9.86) * mm});
            skLineSegment(sketch, "E892", {"start": v(0.42, 9.86) * mm, "end": v(0.5, 10.1) * mm});
            skLineSegment(sketch, "E893", {"start": v(0.5, 10.1) * mm, "end": v(0.61, 10.37) * mm});
            skLineSegment(sketch, "E894", {"start": v(0.61, 10.37) * mm, "end": v(0.79, 10.67) * mm});
            skLineSegment(sketch, "E895", {"start": v(0.79, 10.67) * mm, "end": v(0.94, 10.9) * mm});
            skLineSegment(sketch, "E896", {"start": v(0.94, 10.9) * mm, "end": v(1.09, 11.1) * mm});
            skLineSegment(sketch, "E897", {"start": v(1.09, 11.1) * mm, "end": v(1.22, 11.22) * mm});
            skLineSegment(sketch, "E898", {"start": v(1.22, 11.22) * mm, "end": v(1.28, 11.26) * mm});
            skLineSegment(sketch, "E899", {"start": v(1.28, 11.26) * mm, "end": v(1.3, 11.26) * mm});
            skLineSegment(sketch, "E900", {"start": v(1.3, 11.26) * mm, "end": v(1.32, 11.25) * mm});
            skLineSegment(sketch, "E901", {"start": v(1.32, 11.25) * mm, "end": v(1.33, 11.23) * mm});
            skLineSegment(sketch, "E902", {"start": v(1.33, 11.23) * mm, "end": v(1.33, 11.2) * mm});
            skLineSegment(sketch, "E903", {"start": v(1.33, 11.2) * mm, "end": v(1.34, 11.18) * mm});
            skLineSegment(sketch, "E904", {"start": v(1.34, 11.18) * mm, "end": v(1.36, 11.11) * mm});
            skLineSegment(sketch, "E905", {"start": v(1.36, 11.11) * mm, "end": v(1.4, 11.02) * mm});
            skLineSegment(sketch, "E906", {"start": v(1.4, 11.02) * mm, "end": v(1.67, 11.32) * mm});
            skLineSegment(sketch, "E907", {"start": v(1.67, 11.32) * mm, "end": v(1.8, 11.45) * mm});
            skLineSegment(sketch, "E908", {"start": v(1.8, 11.45) * mm, "end": v(1.9, 11.55) * mm});
            skLineSegment(sketch, "E909", {"start": v(1.9, 11.55) * mm, "end": v(1.97, 11.6) * mm});
            skLineSegment(sketch, "E910", {"start": v(1.97, 11.6) * mm, "end": v(1.98, 11.62) * mm});
            skLineSegment(sketch, "E911", {"start": v(1.98, 11.62) * mm, "end": v(2, 11.62) * mm});
            skLineSegment(sketch, "E912", {"start": v(2, 11.62) * mm, "end": v(2.01, 11.61) * mm});
            skLineSegment(sketch, "E913", {"start": v(2.01, 11.61) * mm, "end": v(2.03, 11.6) * mm});
            skLineSegment(sketch, "E914", {"start": v(2.03, 11.6) * mm, "end": v(2.04, 11.51) * mm});
            skLineSegment(sketch, "E915", {"start": v(2.04, 11.51) * mm, "end": v(2.05, 11.41) * mm});
            skLineSegment(sketch, "E916", {"start": v(2.05, 11.41) * mm, "end": v(2.07, 11.36) * mm});
            skLineSegment(sketch, "E917", {"start": v(2.07, 11.36) * mm, "end": v(2.1, 11.34) * mm});
            skLineSegment(sketch, "E918", {"start": v(2.1, 11.34) * mm, "end": v(2.11, 11.33) * mm});
            skLineSegment(sketch, "E919", {"start": v(2.11, 11.33) * mm, "end": v(2.17, 11.4) * mm});
            skLineSegment(sketch, "E920", {"start": v(2.17, 11.4) * mm, "end": v(2.22, 11.45) * mm});
            skLineSegment(sketch, "E921", {"start": v(2.22, 11.45) * mm, "end": v(2.3, 11.53) * mm});
            skLineSegment(sketch, "E922", {"start": v(2.3, 11.53) * mm, "end": v(2.46, 11.65) * mm});
            skLineSegment(sketch, "E923", {"start": v(2.46, 11.65) * mm, "end": v(2.6, 11.75) * mm});
            skLineSegment(sketch, "E924", {"start": v(2.6, 11.75) * mm, "end": v(2.64, 11.77) * mm});
            skLineSegment(sketch, "E925", {"start": v(2.64, 11.77) * mm, "end": v(2.66, 11.78) * mm});
            skLineSegment(sketch, "E926", {"start": v(2.66, 11.78) * mm, "end": v(2.67, 11.78) * mm});
            skLineSegment(sketch, "E927", {"start": v(2.67, 11.78) * mm, "end": v(2.67, 11.77) * mm});
            skLineSegment(sketch, "E928", {"start": v(2.67, 11.77) * mm, "end": v(2.68, 11.74) * mm});
            skLineSegment(sketch, "E929", {"start": v(2.68, 11.74) * mm, "end": v(2.69, 11.64) * mm});
            skLineSegment(sketch, "E930", {"start": v(2.69, 11.64) * mm, "end": v(2.7, 11.52) * mm});
            skLineSegment(sketch, "E931", {"start": v(2.7, 11.52) * mm, "end": v(2.7, 11.5) * mm});
            skLineSegment(sketch, "E932", {"start": v(2.7, 11.5) * mm, "end": v(2.7, 11.48) * mm});
            skLineSegment(sketch, "E933", {"start": v(2.7, 11.48) * mm, "end": v(2.72, 11.48) * mm});
            skLineSegment(sketch, "E934", {"start": v(2.72, 11.48) * mm, "end": v(2.73, 11.48) * mm});
            skLineSegment(sketch, "E935", {"start": v(2.73, 11.48) * mm, "end": v(2.78, 11.5) * mm});
            skLineSegment(sketch, "E936", {"start": v(2.78, 11.5) * mm, "end": v(2.93, 11.6) * mm});
            skLineSegment(sketch, "E937", {"start": v(2.93, 11.6) * mm, "end": v(3.11, 11.74) * mm});
            skLineSegment(sketch, "E938", {"start": v(3.11, 11.74) * mm, "end": v(3.26, 11.82) * mm});
            skLineSegment(sketch, "E939", {"start": v(3.26, 11.82) * mm, "end": v(3.42, 11.88) * mm});
            skLineSegment(sketch, "E940", {"start": v(3.42, 11.88) * mm, "end": v(3.45, 11.87) * mm});
            skLineSegment(sketch, "E941", {"start": v(3.45, 11.87) * mm, "end": v(3.46, 11.85) * mm});
            skLineSegment(sketch, "E942", {"start": v(3.46, 11.85) * mm, "end": v(3.44, 11.79) * mm});
            skLineSegment(sketch, "E943", {"start": v(3.44, 11.79) * mm, "end": v(3.4, 11.71) * mm});
            skLineSegment(sketch, "E944", {"start": v(3.4, 11.71) * mm, "end": v(3.35, 11.62) * mm});
            skLineSegment(sketch, "E945", {"start": v(3.35, 11.62) * mm, "end": v(3.34, 11.6) * mm});
            skLineSegment(sketch, "E946", {"start": v(3.34, 11.6) * mm, "end": v(3.35, 11.59) * mm});
            skLineSegment(sketch, "E947", {"start": v(3.35, 11.59) * mm, "end": v(3.38, 11.58) * mm});
            skLineSegment(sketch, "E948", {"start": v(3.38, 11.58) * mm, "end": v(3.42, 11.59) * mm});
            skLineSegment(sketch, "E949", {"start": v(3.42, 11.59) * mm, "end": v(3.57, 11.65) * mm});
            skLineSegment(sketch, "E950", {"start": v(3.57, 11.65) * mm, "end": v(3.77, 11.74) * mm});
            skLineSegment(sketch, "E951", {"start": v(3.77, 11.74) * mm, "end": v(3.98, 11.8) * mm});
            skLineSegment(sketch, "E952", {"start": v(3.98, 11.8) * mm, "end": v(4.13, 11.84) * mm});
            skLineSegment(sketch, "E953", {"start": v(4.13, 11.84) * mm, "end": v(4.2, 11.83) * mm});
            skLineSegment(sketch, "E954", {"start": v(4.2, 11.83) * mm, "end": v(4.23, 11.82) * mm});
            skLineSegment(sketch, "E955", {"start": v(4.23, 11.82) * mm, "end": v(4.23, 11.8) * mm});
            skLineSegment(sketch, "E956", {"start": v(4.23, 11.8) * mm, "end": v(4.22, 11.78) * mm});
            skLineSegment(sketch, "E957", {"start": v(4.22, 11.78) * mm, "end": v(4.15, 11.7) * mm});
            skLineSegment(sketch, "E958", {"start": v(4.15, 11.7) * mm, "end": v(4.07, 11.6) * mm});
            skLineSegment(sketch, "E959", {"start": v(4.07, 11.6) * mm, "end": v(4.05, 11.55) * mm});
            skLineSegment(sketch, "E960", {"start": v(4.05, 11.55) * mm, "end": v(4.05, 11.54) * mm});
            skLineSegment(sketch, "E961", {"start": v(4.05, 11.54) * mm, "end": v(4.06, 11.53) * mm});
            skLineSegment(sketch, "E962", {"start": v(4.06, 11.53) * mm, "end": v(4.08, 11.53) * mm});
            skLineSegment(sketch, "E963", {"start": v(4.08, 11.53) * mm, "end": v(4.1, 11.54) * mm});
            skLineSegment(sketch, "E964", {"start": v(4.1, 11.54) * mm, "end": v(4.25, 11.58) * mm});
            skLineSegment(sketch, "E965", {"start": v(4.25, 11.58) * mm, "end": v(4.46, 11.63) * mm});
            skLineSegment(sketch, "E966", {"start": v(4.46, 11.63) * mm, "end": v(4.62, 11.67) * mm});
            skLineSegment(sketch, "E967", {"start": v(4.62, 11.67) * mm, "end": v(4.74, 11.7) * mm});
            skLineSegment(sketch, "E968", {"start": v(4.74, 11.7) * mm, "end": v(4.83, 11.7) * mm});
            skLineSegment(sketch, "E969", {"start": v(4.83, 11.7) * mm, "end": v(4.86, 11.7) * mm});
            skLineSegment(sketch, "E970", {"start": v(4.86, 11.7) * mm, "end": v(4.86, 11.67) * mm});
            skLineSegment(sketch, "E971", {"start": v(4.86, 11.67) * mm, "end": v(4.85, 11.64) * mm});
            skLineSegment(sketch, "E972", {"start": v(4.85, 11.64) * mm, "end": v(4.78, 11.55) * mm});
            skLineSegment(sketch, "E973", {"start": v(4.78, 11.55) * mm, "end": v(4.72, 11.45) * mm});
            skLineSegment(sketch, "E974", {"start": v(4.72, 11.45) * mm, "end": v(4.7, 11.43) * mm});
            skLineSegment(sketch, "E975", {"start": v(4.7, 11.43) * mm, "end": v(4.7, 11.41) * mm});
            skLineSegment(sketch, "E976", {"start": v(4.7, 11.41) * mm, "end": v(4.71, 11.4) * mm});
            skLineSegment(sketch, "E977", {"start": v(4.71, 11.4) * mm, "end": v(4.72, 11.4) * mm});
            skLineSegment(sketch, "E978", {"start": v(4.72, 11.4) * mm, "end": v(4.77, 11.4) * mm});
            skLineSegment(sketch, "E979", {"start": v(4.77, 11.4) * mm, "end": v(5.05, 11.47) * mm});
            skLineSegment(sketch, "E980", {"start": v(5.05, 11.47) * mm, "end": v(5.3, 11.51) * mm});
            skLineSegment(sketch, "E981", {"start": v(5.3, 11.51) * mm, "end": v(5.6, 11.5) * mm});
            skLineSegment(sketch, "E982", {"start": v(5.6, 11.5) * mm, "end": v(5.67, 11.48) * mm});
            skLineSegment(sketch, "E983", {"start": v(5.67, 11.48) * mm, "end": v(5.7, 11.44) * mm});
            skLineSegment(sketch, "E984", {"start": v(5.7, 11.44) * mm, "end": v(5.7, 11.4) * mm});
            skLineSegment(sketch, "E985", {"start": v(5.7, 11.4) * mm, "end": v(5.64, 11.34) * mm});
            skLineSegment(sketch, "E986", {"start": v(5.64, 11.34) * mm, "end": v(5.6, 11.29) * mm});
            skLineSegment(sketch, "E987", {"start": v(5.6, 11.29) * mm, "end": v(5.58, 11.27) * mm});
            skLineSegment(sketch, "E988", {"start": v(5.58, 11.27) * mm, "end": v(5.58, 11.26) * mm});
            skLineSegment(sketch, "E989", {"start": v(5.58, 11.26) * mm, "end": v(5.58, 11.25) * mm});
            skLineSegment(sketch, "E990", {"start": v(5.58, 11.25) * mm, "end": v(5.59, 11.25) * mm});
            skLineSegment(sketch, "E991", {"start": v(5.59, 11.25) * mm, "end": v(5.6, 11.25) * mm});
            skLineSegment(sketch, "E992", {"start": v(5.6, 11.25) * mm, "end": v(5.96, 11.23) * mm});
            skLineSegment(sketch, "E993", {"start": v(5.96, 11.23) * mm, "end": v(6.14, 11.23) * mm});
            skLineSegment(sketch, "E994", {"start": v(6.14, 11.23) * mm, "end": v(6.28, 11.22) * mm});
            skLineSegment(sketch, "E995", {"start": v(6.28, 11.22) * mm, "end": v(6.35, 11.2) * mm});
            skLineSegment(sketch, "E996", {"start": v(6.35, 11.2) * mm, "end": v(6.37, 11.2) * mm});
            skLineSegment(sketch, "E997", {"start": v(6.37, 11.2) * mm, "end": v(6.37, 11.2) * mm});
            skLineSegment(sketch, "E998", {"start": v(6.37, 11.2) * mm, "end": v(6.38, 11.18) * mm});
            skLineSegment(sketch, "E999", {"start": v(6.38, 11.18) * mm, "end": v(6.37, 11.16) * mm});
            skLineSegment(sketch, "E1000", {"start": v(6.37, 11.16) * mm, "end": v(6.36, 11.12) * mm});
            skLineSegment(sketch, "E1001", {"start": v(6.36, 11.12) * mm, "end": v(6.32, 11.04) * mm});
            skLineSegment(sketch, "E1002", {"start": v(6.32, 11.04) * mm, "end": v(6.16, 10.77) * mm});
            skLineSegment(sketch, "E1003", {"start": v(6.16, 10.77) * mm, "end": v(6.08, 10.59) * mm});
            skLineSegment(sketch, "E1004", {"start": v(6.08, 10.59) * mm, "end": v(6.07, 10.55) * mm});
            skLineSegment(sketch, "E1005", {"start": v(6.07, 10.55) * mm, "end": v(6.08, 10.53) * mm});
            skLineSegment(sketch, "E1006", {"start": v(6.08, 10.53) * mm, "end": v(6.1, 10.52) * mm});
            skLineSegment(sketch, "E1007", {"start": v(6.1, 10.52) * mm, "end": v(6.14, 10.52) * mm});
            skLineSegment(sketch, "E1008", {"start": v(6.14, 10.52) * mm, "end": v(6.24, 10.51) * mm});
            skLineSegment(sketch, "E1009", {"start": v(6.24, 10.51) * mm, "end": v(6.38, 10.5) * mm});
            skLineSegment(sketch, "E1010", {"start": v(6.38, 10.5) * mm, "end": v(6.41, 10.5) * mm});
            skLineSegment(sketch, "E1011", {"start": v(6.41, 10.5) * mm, "end": v(6.42, 10.47) * mm});
            skLineSegment(sketch, "E1012", {"start": v(6.42, 10.47) * mm, "end": v(6.39, 10.38) * mm});
            skLineSegment(sketch, "E1013", {"start": v(6.39, 10.38) * mm, "end": v(6.31, 10.28) * mm});
            skLineSegment(sketch, "E1014", {"start": v(6.31, 10.28) * mm, "end": v(6.1, 10.05) * mm});
            skLineSegment(sketch, "E1015", {"start": v(6.1, 10.05) * mm, "end": v(5.89, 9.86) * mm});
            skLineSegment(sketch, "E1016", {"start": v(5.89, 9.86) * mm, "end": v(6.07, 9.87) * mm});
            skLineSegment(sketch, "E1017", {"start": v(6.07, 9.87) * mm, "end": v(6.22, 9.87) * mm});
            skLineSegment(sketch, "E1018", {"start": v(6.22, 9.87) * mm, "end": v(6.26, 9.87) * mm});
            skLineSegment(sketch, "E1019", {"start": v(6.26, 9.87) * mm, "end": v(6.27, 9.86) * mm});
            skLineSegment(sketch, "E1020", {"start": v(6.27, 9.86) * mm, "end": v(6.28, 9.86) * mm});
            skLineSegment(sketch, "E1021", {"start": v(6.28, 9.86) * mm, "end": v(6.27, 9.8) * mm});
            skLineSegment(sketch, "E1022", {"start": v(6.27, 9.8) * mm, "end": v(6.21, 9.7) * mm});
            skLineSegment(sketch, "E1023", {"start": v(6.21, 9.7) * mm, "end": v(5.97, 9.43) * mm});
            skLineSegment(sketch, "E1024", {"start": v(5.97, 9.43) * mm, "end": v(5.84, 9.3) * mm});
            skLineSegment(sketch, "E1025", {"start": v(5.84, 9.3) * mm, "end": v(5.82, 9.24) * mm});
            skLineSegment(sketch, "E1026", {"start": v(5.82, 9.24) * mm, "end": v(5.81, 9.22) * mm});
            skLineSegment(sketch, "E1027", {"start": v(5.81, 9.22) * mm, "end": v(5.82, 9.2) * mm});
            skLineSegment(sketch, "E1028", {"start": v(5.82, 9.2) * mm, "end": v(5.84, 9.2) * mm});
            skLineSegment(sketch, "E1029", {"start": v(5.84, 9.2) * mm, "end": v(5.94, 9.2) * mm});
            skLineSegment(sketch, "E1030", {"start": v(5.94, 9.2) * mm, "end": v(6.01, 9.2) * mm});
            skLineSegment(sketch, "E1031", {"start": v(6.01, 9.2) * mm, "end": v(6.03, 9.2) * mm});
            skLineSegment(sketch, "E1032", {"start": v(6.03, 9.2) * mm, "end": v(6.03, 9.16) * mm});
            skLineSegment(sketch, "E1033", {"start": v(6.03, 9.16) * mm, "end": v(6.01, 9.11) * mm});
            skLineSegment(sketch, "E1034", {"start": v(6.01, 9.11) * mm, "end": v(5.98, 9.07) * mm});
            skLineSegment(sketch, "E1035", {"start": v(5.98, 9.07) * mm, "end": v(5.87, 8.95) * mm});
            skLineSegment(sketch, "E1036", {"start": v(5.87, 8.95) * mm, "end": v(5.55, 8.7) * mm});
            skLineSegment(sketch, "E1037", {"start": v(5.55, 8.7) * mm, "end": v(5.41, 8.6) * mm});
            skLineSegment(sketch, "E1038", {"start": v(5.41, 8.6) * mm, "end": v(5.55, 8.6) * mm});
            skLineSegment(sketch, "E1039", {"start": v(5.55, 8.6) * mm, "end": v(5.67, 8.57) * mm});
            skLineSegment(sketch, "E1040", {"start": v(5.67, 8.57) * mm, "end": v(5.7, 8.54) * mm});
            skLineSegment(sketch, "E1041", {"start": v(5.7, 8.54) * mm, "end": v(5.7, 8.5) * mm});
            skLineSegment(sketch, "E1042", {"start": v(5.7, 8.5) * mm, "end": v(5.66, 8.46) * mm});
            skLineSegment(sketch, "E1043", {"start": v(5.66, 8.46) * mm, "end": v(5.52, 8.35) * mm});
            skLineSegment(sketch, "E1044", {"start": v(5.52, 8.35) * mm, "end": v(5.3, 8.2) * mm});
            skLineSegment(sketch, "E1045", {"start": v(5.3, 8.2) * mm, "end": v(5.12, 8.11) * mm});
            skLineSegment(sketch, "E1046", {"start": v(5.12, 8.11) * mm, "end": v(4.91, 8) * mm});
            skLineSegment(sketch, "E1047", {"start": v(4.91, 8) * mm, "end": v(5.05, 7.97) * mm});
            skLineSegment(sketch, "E1048", {"start": v(5.05, 7.97) * mm, "end": v(5.15, 7.93) * mm});
            skLineSegment(sketch, "E1049", {"start": v(5.15, 7.93) * mm, "end": v(5.18, 7.92) * mm});
            skLineSegment(sketch, "E1050", {"start": v(5.18, 7.92) * mm, "end": v(5.2, 7.9) * mm});
            skLineSegment(sketch, "E1051", {"start": v(5.2, 7.9) * mm, "end": v(5.16, 7.85) * mm});
            skLineSegment(sketch, "E1052", {"start": v(5.16, 7.85) * mm, "end": v(5.05, 7.79) * mm});
            skLineSegment(sketch, "E1053", {"start": v(5.05, 7.79) * mm, "end": v(4.68, 7.64) * mm});
            skText(sketch, "E1054", { "text": "LED", "fontName": "OpenSans-Bold.ttf"});
            skCircle(sketch, "E1055", {"center": v(73.5, 0) * mm, "radius": 0.97 * mm});
            skCircle(sketch, "E1056", {"center": v(73.5, 0) * mm, "radius": 0.68 * mm});
            skLineSegment(sketch, "E1057", {"start": v(72.65, -0.47) * mm, "end": v(69.26, -3.28) * mm});
            skArc(sketch, "E1058", {"start": v(69.26, -3.28) * mm, "mid": v(69.26, -4.25) * mm, "end": v(70.22, -4.25) * mm});
            skLineSegment(sketch, "E1059", {"start": v(70.22, -4.25) * mm, "end": v(73.04, -0.85) * mm});
            skLineSegment(sketch, "E1060", {"start": v(72.65, 0.46) * mm, "end": v(69.26, 3.28) * mm});
            skArc(sketch, "E1061", {"start": v(69.26, 3.28) * mm, "mid": v(69.26, 4.24) * mm, "end": v(70.22, 4.24) * mm});
            skLineSegment(sketch, "E1062", {"start": v(70.22, 4.24) * mm, "end": v(73.04, 0.85) * mm});
            skLineSegment(sketch, "E1063", {"start": v(73.97, -0.85) * mm, "end": v(76.78, -4.25) * mm});
            skArc(sketch, "E1064", {"start": v(76.78, -4.25) * mm, "mid": v(77.75, -4.25) * mm, "end": v(77.75, -3.28) * mm});
            skLineSegment(sketch, "E1065", {"start": v(77.75, -3.28) * mm, "end": v(74.35, -0.47) * mm});
            skLineSegment(sketch, "E1066", {"start": v(74.35, 0.46) * mm, "end": v(77.75, 3.28) * mm});
            skArc(sketch, "E1067", {"start": v(77.75, 3.28) * mm, "mid": v(77.75, 4.24) * mm, "end": v(76.78, 4.24) * mm});
            skLineSegment(sketch, "E1068", {"start": v(76.78, 4.24) * mm, "end": v(73.97, 0.85) * mm});
            skCircle(sketch, "E1069", {"center": v(73.5, 0) * mm, "radius": 6.3 * mm});
            skCircle(sketch, "E1070", {"center": v(73.5, 0) * mm, "radius": 6.58 * mm});
            skLineSegment(sketch, "E1071", {"start": v(-78.36, 4.44) * mm, "end": v(-78.36, 0.07) * mm});
            skLineSegment(sketch, "E1072", {"start": v(-66.4, -5.46) * mm, "end": v(-66.4, -5.5) * mm});
            skLineSegment(sketch, "E1073", {"start": v(-66.3, -5.04) * mm, "end": v(-66.37, -5.26) * mm});
            skLineSegment(sketch, "E1074", {"start": v(-66.37, -5.26) * mm, "end": v(-66.4, -5.46) * mm});
            skLineSegment(sketch, "E1075", {"start": v(-66, -4.88) * mm, "end": v(-66.2, -4.93) * mm});
            skLineSegment(sketch, "E1076", {"start": v(-66.2, -4.93) * mm, "end": v(-66.3, -5.04) * mm});
            skLineSegment(sketch, "E1077", {"start": v(-65.7, -5.04) * mm, "end": v(-65.84, -4.91) * mm});
            skLineSegment(sketch, "E1078", {"start": v(-65.84, -4.91) * mm, "end": v(-66, -4.88) * mm});
            skLineSegment(sketch, "E1079", {"start": v(-65.6, -5.46) * mm, "end": v(-65.64, -5.2) * mm});
            skLineSegment(sketch, "E1080", {"start": v(-65.64, -5.2) * mm, "end": v(-65.7, -5.04) * mm});
            skLineSegment(sketch, "E1081", {"start": v(-65.6, -5.5) * mm, "end": v(-65.6, -5.46) * mm});
            skLineSegment(sketch, "E1082", {"start": v(-65.7, -5.93) * mm, "end": v(-65.62, -5.71) * mm});
            skLineSegment(sketch, "E1083", {"start": v(-65.62, -5.71) * mm, "end": v(-65.6, -5.5) * mm});
            skLineSegment(sketch, "E1084", {"start": v(-66, -6.09) * mm, "end": v(-65.8, -6.04) * mm});
            skLineSegment(sketch, "E1085", {"start": v(-65.8, -6.04) * mm, "end": v(-65.7, -5.93) * mm});
            skLineSegment(sketch, "E1086", {"start": v(-66.3, -5.93) * mm, "end": v(-66.16, -6.06) * mm});
            skLineSegment(sketch, "E1087", {"start": v(-66.16, -6.06) * mm, "end": v(-66, -6.09) * mm});
            skLineSegment(sketch, "E1088", {"start": v(-66.4, -5.5) * mm, "end": v(-66.36, -5.77) * mm});
            skLineSegment(sketch, "E1089", {"start": v(-66.36, -5.77) * mm, "end": v(-66.3, -5.93) * mm});
            skLineSegment(sketch, "E1090", {"start": v(-66.92, -5.5) * mm, "end": v(-66.92, -5.46) * mm});
            skLineSegment(sketch, "E1091", {"start": v(-66.67, -6.22) * mm, "end": v(-66.79, -6.05) * mm});
            skLineSegment(sketch, "E1092", {"start": v(-66.79, -6.05) * mm, "end": v(-66.87, -5.86) * mm});
            skLineSegment(sketch, "E1093", {"start": v(-66.87, -5.86) * mm, "end": v(-66.92, -5.5) * mm});
            skLineSegment(sketch, "E1094", {"start": v(-66, -6.5) * mm, "end": v(-66.22, -6.47) * mm});
            skLineSegment(sketch, "E1095", {"start": v(-66.22, -6.47) * mm, "end": v(-66.42, -6.4) * mm});
            skLineSegment(sketch, "E1096", {"start": v(-66.42, -6.4) * mm, "end": v(-66.67, -6.22) * mm});
            skLineSegment(sketch, "E1097", {"start": v(-65.33, -6.22) * mm, "end": v(-65.48, -6.35) * mm});
            skLineSegment(sketch, "E1098", {"start": v(-65.48, -6.35) * mm, "end": v(-65.66, -6.44) * mm});
            skLineSegment(sketch, "E1099", {"start": v(-65.66, -6.44) * mm, "end": v(-66, -6.5) * mm});
            skLineSegment(sketch, "E1100", {"start": v(-65.08, -5.5) * mm, "end": v(-65.1, -5.74) * mm});
            skLineSegment(sketch, "E1101", {"start": v(-65.1, -5.74) * mm, "end": v(-65.16, -5.94) * mm});
            skLineSegment(sketch, "E1102", {"start": v(-65.16, -5.94) * mm, "end": v(-65.33, -6.22) * mm});
            skLineSegment(sketch, "E1103", {"start": v(-65.08, -5.46) * mm, "end": v(-65.08, -5.5) * mm});
            skLineSegment(sketch, "E1104", {"start": v(-65.33, -4.75) * mm, "end": v(-65.2, -4.92) * mm});
            skLineSegment(sketch, "E1105", {"start": v(-65.2, -4.92) * mm, "end": v(-65.13, -5.11) * mm});
            skLineSegment(sketch, "E1106", {"start": v(-65.13, -5.11) * mm, "end": v(-65.08, -5.46) * mm});
            skLineSegment(sketch, "E1107", {"start": v(-66, -4.48) * mm, "end": v(-65.77, -4.5) * mm});
            skLineSegment(sketch, "E1108", {"start": v(-65.77, -4.5) * mm, "end": v(-65.58, -4.56) * mm});
            skLineSegment(sketch, "E1109", {"start": v(-65.58, -4.56) * mm, "end": v(-65.33, -4.75) * mm});
            skLineSegment(sketch, "E1110", {"start": v(-66.67, -4.75) * mm, "end": v(-66.52, -4.62) * mm});
            skLineSegment(sketch, "E1111", {"start": v(-66.52, -4.62) * mm, "end": v(-66.34, -4.53) * mm});
            skLineSegment(sketch, "E1112", {"start": v(-66.34, -4.53) * mm, "end": v(-66, -4.48) * mm});
            skLineSegment(sketch, "E1113", {"start": v(-66.92, -5.46) * mm, "end": v(-66.9, -5.23) * mm});
            skLineSegment(sketch, "E1114", {"start": v(-66.9, -5.23) * mm, "end": v(-66.84, -5.03) * mm});
            skLineSegment(sketch, "E1115", {"start": v(-66.84, -5.03) * mm, "end": v(-66.67, -4.75) * mm});
            skLineSegment(sketch, "E1116", {"start": v(-67.86, -4.02) * mm, "end": v(-68.14, -3.97) * mm});
            skLineSegment(sketch, "E1117", {"start": v(-67.86, -6.09) * mm, "end": v(-67.86, -4.02) * mm});
            skLineSegment(sketch, "E1118", {"start": v(-68.12, -6.14) * mm, "end": v(-67.86, -6.09) * mm});
            skLineSegment(sketch, "E1119", {"start": v(-68.12, -6.45) * mm, "end": v(-68.12, -6.14) * mm});
            skLineSegment(sketch, "E1120", {"start": v(-67.09, -6.45) * mm, "end": v(-68.12, -6.45) * mm});
            skLineSegment(sketch, "E1121", {"start": v(-67.09, -6.14) * mm, "end": v(-67.09, -6.45) * mm});
            skLineSegment(sketch, "E1122", {"start": v(-67.34, -6.09) * mm, "end": v(-67.09, -6.14) * mm});
            skLineSegment(sketch, "E1123", {"start": v(-67.34, -3.65) * mm, "end": v(-67.34, -6.09) * mm});
            skLineSegment(sketch, "E1124", {"start": v(-68.14, -3.65) * mm, "end": v(-67.34, -3.65) * mm});
            skLineSegment(sketch, "E1125", {"start": v(-68.14, -3.97) * mm, "end": v(-68.14, -3.65) * mm});
            skLineSegment(sketch, "E1126", {"start": v(-68.51, -3.65) * mm, "end": v(-68.51, -4.05) * mm});
            skLineSegment(sketch, "E1127", {"start": v(-69.04, -3.65) * mm, "end": v(-68.51, -3.65) * mm});
            skLineSegment(sketch, "E1128", {"start": v(-69.04, -4.05) * mm, "end": v(-69.04, -3.65) * mm});
            skLineSegment(sketch, "E1129", {"start": v(-68.51, -4.05) * mm, "end": v(-69.04, -4.05) * mm});
            skLineSegment(sketch, "E1130", {"start": v(-69.29, -6.45) * mm, "end": v(-69.29, -6.14) * mm});
            skLineSegment(sketch, "E1131", {"start": v(-68.26, -6.45) * mm, "end": v(-69.29, -6.45) * mm});
            skLineSegment(sketch, "E1132", {"start": v(-68.26, -6.14) * mm, "end": v(-68.26, -6.45) * mm});
            skLineSegment(sketch, "E1133", {"start": v(-68.51, -6.09) * mm, "end": v(-68.26, -6.14) * mm});
            skLineSegment(sketch, "E1134", {"start": v(-68.51, -4.51) * mm, "end": v(-68.51, -6.09) * mm});
            skLineSegment(sketch, "E1135", {"start": v(-69.32, -4.51) * mm, "end": v(-68.51, -4.51) * mm});
            skLineSegment(sketch, "E1136", {"start": v(-69.32, -4.83) * mm, "end": v(-69.32, -4.51) * mm});
            skLineSegment(sketch, "E1137", {"start": v(-69.04, -4.88) * mm, "end": v(-69.32, -4.83) * mm});
            skLineSegment(sketch, "E1138", {"start": v(-69.04, -6.09) * mm, "end": v(-69.04, -4.88) * mm});
            skLineSegment(sketch, "E1139", {"start": v(-69.29, -6.14) * mm, "end": v(-69.04, -6.09) * mm});
            skLineSegment(sketch, "E1140", {"start": v(-70.81, -5.5) * mm, "end": v(-70.81, -5.54) * mm});
            skLineSegment(sketch, "E1141", {"start": v(-70.73, -5.05) * mm, "end": v(-70.8, -5.28) * mm});
            skLineSegment(sketch, "E1142", {"start": v(-70.8, -5.28) * mm, "end": v(-70.81, -5.5) * mm});
            skLineSegment(sketch, "E1143", {"start": v(-70.45, -4.88) * mm, "end": v(-70.63, -4.94) * mm});
            skLineSegment(sketch, "E1144", {"start": v(-70.63, -4.94) * mm, "end": v(-70.73, -5.05) * mm});
            skLineSegment(sketch, "E1145", {"start": v(-70.25, -4.93) * mm, "end": v(-70.35, -4.9) * mm});
            skLineSegment(sketch, "E1146", {"start": v(-70.35, -4.9) * mm, "end": v(-70.45, -4.88) * mm});
            skLineSegment(sketch, "E1147", {"start": v(-70.11, -5.07) * mm, "end": v(-70.18, -4.98) * mm});
            skLineSegment(sketch, "E1148", {"start": v(-70.18, -4.98) * mm, "end": v(-70.25, -4.93) * mm});
            skLineSegment(sketch, "E1149", {"start": v(-70.11, -5.91) * mm, "end": v(-70.11, -5.07) * mm});
            skLineSegment(sketch, "E1150", {"start": v(-70.25, -6.04) * mm, "end": v(-70.16, -5.98) * mm});
            skLineSegment(sketch, "E1151", {"start": v(-70.16, -5.98) * mm, "end": v(-70.11, -5.91) * mm});
            skLineSegment(sketch, "E1152", {"start": v(-70.45, -6.08) * mm, "end": v(-70.33, -6.07) * mm});
            skLineSegment(sketch, "E1153", {"start": v(-70.33, -6.07) * mm, "end": v(-70.25, -6.04) * mm});
            skLineSegment(sketch, "E1154", {"start": v(-70.73, -5.94) * mm, "end": v(-70.6, -6.06) * mm});
            skLineSegment(sketch, "E1155", {"start": v(-70.6, -6.06) * mm, "end": v(-70.45, -6.08) * mm});
            skLineSegment(sketch, "E1156", {"start": v(-70.81, -5.54) * mm, "end": v(-70.79, -5.79) * mm});
            skLineSegment(sketch, "E1157", {"start": v(-70.79, -5.79) * mm, "end": v(-70.73, -5.94) * mm});
            skLineSegment(sketch, "E1158", {"start": v(-73.1, -6.14) * mm, "end": v(-73.1, -6.45) * mm});
            skLineSegment(sketch, "E1159", {"start": v(-73.26, -6.12) * mm, "end": v(-73.1, -6.14) * mm});
            skLineSegment(sketch, "E1160", {"start": v(-73.26, -6.04) * mm, "end": v(-73.26, -6.09) * mm});
            skLineSegment(sketch, "E1161", {"start": v(-73.26, -6.09) * mm, "end": v(-73.26, -6.12) * mm});
            skLineSegment(sketch, "E1162", {"start": v(-73.26, -5.96) * mm, "end": v(-73.26, -6) * mm});
            skLineSegment(sketch, "E1163", {"start": v(-73.26, -6) * mm, "end": v(-73.26, -6.04) * mm});
            skLineSegment(sketch, "E1164", {"start": v(-73.26, -5.16) * mm, "end": v(-73.26, -5.96) * mm});
            skLineSegment(sketch, "E1165", {"start": v(-73.49, -4.65) * mm, "end": v(-73.3, -4.9) * mm});
            skLineSegment(sketch, "E1166", {"start": v(-73.3, -4.9) * mm, "end": v(-73.26, -5.16) * mm});
            skLineSegment(sketch, "E1167", {"start": v(-74.07, -4.48) * mm, "end": v(-73.71, -4.53) * mm});
            skLineSegment(sketch, "E1168", {"start": v(-73.71, -4.53) * mm, "end": v(-73.49, -4.65) * mm});
            skLineSegment(sketch, "E1169", {"start": v(-74.48, -4.54) * mm, "end": v(-74.26, -4.49) * mm});
            skLineSegment(sketch, "E1170", {"start": v(-74.26, -4.49) * mm, "end": v(-74.07, -4.48) * mm});
            skLineSegment(sketch, "E1171", {"start": v(-74.8, -4.7) * mm, "end": v(-74.63, -4.6) * mm});
            skLineSegment(sketch, "E1172", {"start": v(-74.63, -4.6) * mm, "end": v(-74.48, -4.54) * mm});
            skLineSegment(sketch, "E1173", {"start": v(-74.8, -5.14) * mm, "end": v(-74.8, -4.7) * mm});
            skLineSegment(sketch, "E1174", {"start": v(-73.1, -6.45) * mm, "end": v(-73.7, -6.45) * mm});
            skLineSegment(sketch, "E1175", {"start": v(-74.15, -6.1) * mm, "end": v(-74.03, -6.09) * mm});
            skLineSegment(sketch, "E1176", {"start": v(-74.03, -6.09) * mm, "end": v(-73.94, -6.05) * mm});
            skLineSegment(sketch, "E1177", {"start": v(-73.94, -6.05) * mm, "end": v(-73.84, -5.99) * mm});
            skLineSegment(sketch, "E1178", {"start": v(-73.84, -5.99) * mm, "end": v(-73.79, -5.92) * mm});
            skLineSegment(sketch, "E1179", {"start": v(-73.79, -5.92) * mm, "end": v(-73.79, -5.63) * mm});
            skLineSegment(sketch, "E1180", {"start": v(-73.79, -5.63) * mm, "end": v(-74.06, -5.63) * mm});
            skLineSegment(sketch, "E1181", {"start": v(-74.06, -5.63) * mm, "end": v(-74.22, -5.65) * mm});
            skLineSegment(sketch, "E1182", {"start": v(-74.22, -5.65) * mm, "end": v(-74.3, -5.7) * mm});
            skLineSegment(sketch, "E1183", {"start": v(-74.3, -5.7) * mm, "end": v(-74.38, -5.8) * mm});
            skLineSegment(sketch, "E1184", {"start": v(-74.38, -5.8) * mm, "end": v(-74.4, -5.9) * mm});
            skLineSegment(sketch, "E1185", {"start": v(-74.4, -5.9) * mm, "end": v(-74.37, -6) * mm});
            skLineSegment(sketch, "E1186", {"start": v(-74.37, -6) * mm, "end": v(-74.33, -6.05) * mm});
            skLineSegment(sketch, "E1187", {"start": v(-70.14, 3.51) * mm, "end": v(-68.28, 2.68) * mm});
            skLineSegment(sketch, "E1188", {"start": v(-71.01, -6.72) * mm, "end": v(-70.87, -6.77) * mm});
            skLineSegment(sketch, "E1189", {"start": v(-70.87, -6.77) * mm, "end": v(-70.76, -6.8) * mm});
            skLineSegment(sketch, "E1190", {"start": v(-68.28, 2.68) * mm, "end": v(-63.6, 4.84) * mm});
            skLineSegment(sketch, "E1191", {"start": v(-70.76, -6.8) * mm, "end": v(-70.61, -6.83) * mm});
            skLineSegment(sketch, "E1192", {"start": v(-70.61, -6.83) * mm, "end": v(-70.5, -6.84) * mm});
            skLineSegment(sketch, "E1193", {"start": v(-63.6, 4.84) * mm, "end": v(-70.14, 7.83) * mm});
            skLineSegment(sketch, "E1194", {"start": v(-70.5, -6.84) * mm, "end": v(-70.3, -6.8) * mm});
            skLineSegment(sketch, "E1195", {"start": v(-70.3, -6.8) * mm, "end": v(-70.2, -6.72) * mm});
            skLineSegment(sketch, "E1196", {"start": v(-76.08, -3.84) * mm, "end": v(-75.85, -3.86) * mm});
            skLineSegment(sketch, "E1197", {"start": v(-75.85, -3.86) * mm, "end": v(-75.64, -3.91) * mm});
            skLineSegment(sketch, "E1198", {"start": v(-75.64, -3.91) * mm, "end": v(-75.38, -4.07) * mm});
            skLineSegment(sketch, "E1199", {"start": v(-71.14, -6.23) * mm, "end": v(-71.3, -5.88) * mm});
            skLineSegment(sketch, "E1200", {"start": v(-71.3, -5.88) * mm, "end": v(-71.34, -5.54) * mm});
            skLineSegment(sketch, "E1201", {"start": v(-75.38, -4.07) * mm, "end": v(-75.25, -4.21) * mm});
            skLineSegment(sketch, "E1202", {"start": v(-75.25, -4.21) * mm, "end": v(-75.17, -4.37) * mm});
            skLineSegment(sketch, "E1203", {"start": v(-75.17, -4.37) * mm, "end": v(-75.12, -4.68) * mm});
            skLineSegment(sketch, "E1204", {"start": v(-71.34, -5.54) * mm, "end": v(-71.34, -5.5) * mm});
            skLineSegment(sketch, "E1205", {"start": v(-75.12, -4.68) * mm, "end": v(-75.14, -4.87) * mm});
            skLineSegment(sketch, "E1206", {"start": v(-75.14, -4.87) * mm, "end": v(-75.2, -5.05) * mm});
            skLineSegment(sketch, "E1207", {"start": v(-75.2, -5.05) * mm, "end": v(-75.38, -5.28) * mm});
            skLineSegment(sketch, "E1208", {"start": v(-75.38, -5.28) * mm, "end": v(-75.54, -5.39) * mm});
            skLineSegment(sketch, "E1209", {"start": v(-75.54, -5.39) * mm, "end": v(-75.73, -5.46) * mm});
            skLineSegment(sketch, "E1210", {"start": v(-75.73, -5.46) * mm, "end": v(-76.08, -5.5) * mm});
            skLineSegment(sketch, "E1211", {"start": v(-76.08, -5.5) * mm, "end": v(-76.52, -5.5) * mm});
            skLineSegment(sketch, "E1212", {"start": v(-76.52, -5.5) * mm, "end": v(-76.52, -6.09) * mm});
            skLineSegment(sketch, "E1213", {"start": v(-76.52, -6.09) * mm, "end": v(-76.25, -6.14) * mm});
            skLineSegment(sketch, "E1214", {"start": v(-76.25, -6.14) * mm, "end": v(-76.25, -6.45) * mm});
            skLineSegment(sketch, "E1215", {"start": v(-76.25, -6.45) * mm, "end": v(-77.33, -6.45) * mm});
            skLineSegment(sketch, "E1216", {"start": v(-77.33, -6.45) * mm, "end": v(-77.33, -6.14) * mm});
            skLineSegment(sketch, "E1217", {"start": v(-77.33, -6.14) * mm, "end": v(-77.05, -6.09) * mm});
            skLineSegment(sketch, "E1218", {"start": v(-77.05, -6.09) * mm, "end": v(-77.05, -4.21) * mm});
            skLineSegment(sketch, "E1219", {"start": v(-77.05, -4.21) * mm, "end": v(-77.33, -4.16) * mm});
            skLineSegment(sketch, "E1220", {"start": v(-77.33, -4.16) * mm, "end": v(-77.33, -3.84) * mm});
            skLineSegment(sketch, "E1221", {"start": v(-77.33, -3.84) * mm, "end": v(-77.05, -3.84) * mm});
            skLineSegment(sketch, "E1222", {"start": v(-77.05, -3.84) * mm, "end": v(-76.08, -3.84) * mm});
            skLineSegment(sketch, "E1223", {"start": v(-76.52, -5.1) * mm, "end": v(-76.08, -5.1) * mm});
            skLineSegment(sketch, "E1224", {"start": v(-74.92, -5.91) * mm, "end": v(-74.85, -5.65) * mm});
            skLineSegment(sketch, "E1225", {"start": v(-74.85, -5.65) * mm, "end": v(-74.7, -5.5) * mm});
            skLineSegment(sketch, "E1226", {"start": v(-74.7, -5.5) * mm, "end": v(-74.39, -5.37) * mm});
            skLineSegment(sketch, "E1227", {"start": v(-74.39, -5.37) * mm, "end": v(-74.06, -5.34) * mm});
            skLineSegment(sketch, "E1228", {"start": v(-74.06, -5.34) * mm, "end": v(-73.79, -5.34) * mm});
            skLineSegment(sketch, "E1229", {"start": v(-73.79, -5.34) * mm, "end": v(-73.79, -5.15) * mm});
            skLineSegment(sketch, "E1230", {"start": v(-73.79, -5.15) * mm, "end": v(-73.81, -5.02) * mm});
            skLineSegment(sketch, "E1231", {"start": v(-73.81, -5.02) * mm, "end": v(-73.87, -4.94) * mm});
            skLineSegment(sketch, "E1232", {"start": v(-73.87, -4.94) * mm, "end": v(-73.98, -4.87) * mm});
            skLineSegment(sketch, "E1233", {"start": v(-73.98, -4.87) * mm, "end": v(-74.1, -4.86) * mm});
            skLineSegment(sketch, "E1234", {"start": v(-70.14, 7.83) * mm, "end": v(-70.14, 3.51) * mm});
            skLineSegment(sketch, "E1235", {"start": v(-71.1, -7.09) * mm, "end": v(-71.01, -6.72) * mm});
            skLineSegment(sketch, "E1236", {"start": v(-74.41, -5.14) * mm, "end": v(-74.8, -5.14) * mm});
            skLineSegment(sketch, "E1237", {"start": v(-71.14, 7.76) * mm, "end": v(-77.68, 4.84) * mm});
            skLineSegment(sketch, "E1238", {"start": v(-70.8, -7.2) * mm, "end": v(-70.98, -7.14) * mm});
            skLineSegment(sketch, "E1239", {"start": v(-70.98, -7.14) * mm, "end": v(-71.1, -7.09) * mm});
            skLineSegment(sketch, "E1240", {"start": v(-74.38, -4.93) * mm, "end": v(-74.41, -5.14) * mm});
            skLineSegment(sketch, "E1241", {"start": v(-71.14, 3.51) * mm, "end": v(-71.14, 7.76) * mm});
            skLineSegment(sketch, "E1242", {"start": v(-70.5, -7.24) * mm, "end": v(-70.66, -7.23) * mm});
            skLineSegment(sketch, "E1243", {"start": v(-70.66, -7.23) * mm, "end": v(-70.8, -7.2) * mm});
            skLineSegment(sketch, "E1244", {"start": v(-74.27, -4.88) * mm, "end": v(-74.34, -4.9) * mm});
            skLineSegment(sketch, "E1245", {"start": v(-74.34, -4.9) * mm, "end": v(-74.38, -4.93) * mm});
            skLineSegment(sketch, "E1246", {"start": v(-72.98, 2.66) * mm, "end": v(-71.14, 3.51) * mm});
            skLineSegment(sketch, "E1247", {"start": v(-69.83, -7) * mm, "end": v(-69.98, -7.12) * mm});
            skLineSegment(sketch, "E1248", {"start": v(-69.98, -7.12) * mm, "end": v(-70.15, -7.2) * mm});
            skLineSegment(sketch, "E1249", {"start": v(-70.15, -7.2) * mm, "end": v(-70.5, -7.24) * mm});
            skLineSegment(sketch, "E1250", {"start": v(-74.1, -4.86) * mm, "end": v(-74.2, -4.87) * mm});
            skLineSegment(sketch, "E1251", {"start": v(-74.2, -4.87) * mm, "end": v(-74.27, -4.88) * mm});
            skLineSegment(sketch, "E1252", {"start": v(-74.75, -6.34) * mm, "end": v(-74.88, -6.13) * mm});
            skLineSegment(sketch, "E1253", {"start": v(-74.88, -6.13) * mm, "end": v(-74.92, -5.91) * mm});
            skLineSegment(sketch, "E1254", {"start": v(-74.3, -6.5) * mm, "end": v(-74.58, -6.44) * mm});
            skLineSegment(sketch, "E1255", {"start": v(-74.58, -6.44) * mm, "end": v(-74.75, -6.34) * mm});
            skLineSegment(sketch, "E1256", {"start": v(-74, -6.42) * mm, "end": v(-74.15, -6.48) * mm});
            skLineSegment(sketch, "E1257", {"start": v(-74.15, -6.48) * mm, "end": v(-74.3, -6.5) * mm});
            skLineSegment(sketch, "E1258", {"start": v(-73.76, -6.25) * mm, "end": v(-73.88, -6.36) * mm});
            skLineSegment(sketch, "E1259", {"start": v(-73.88, -6.36) * mm, "end": v(-74, -6.42) * mm});
            skLineSegment(sketch, "E1260", {"start": v(-73.74, -6.35) * mm, "end": v(-73.75, -6.3) * mm});
            skLineSegment(sketch, "E1261", {"start": v(-73.75, -6.3) * mm, "end": v(-73.76, -6.25) * mm});
            skLineSegment(sketch, "E1262", {"start": v(-73.7, -6.45) * mm, "end": v(-73.72, -6.4) * mm});
            skLineSegment(sketch, "E1263", {"start": v(-73.72, -6.4) * mm, "end": v(-73.74, -6.35) * mm});
            skLineSegment(sketch, "E1264", {"start": v(-76.52, -4.24) * mm, "end": v(-76.52, -5.1) * mm});
            skLineSegment(sketch, "E1265", {"start": v(-76.08, -4.24) * mm, "end": v(-76.52, -4.24) * mm});
            skLineSegment(sketch, "E1266", {"start": v(-75.75, -4.37) * mm, "end": v(-75.91, -4.27) * mm});
            skLineSegment(sketch, "E1267", {"start": v(-75.91, -4.27) * mm, "end": v(-76.08, -4.24) * mm});
            skLineSegment(sketch, "E1268", {"start": v(-75.64, -4.68) * mm, "end": v(-75.68, -4.49) * mm});
            skLineSegment(sketch, "E1269", {"start": v(-75.68, -4.49) * mm, "end": v(-75.75, -4.37) * mm});
            skLineSegment(sketch, "E1270", {"start": v(-75.75, -4.98) * mm, "end": v(-75.66, -4.83) * mm});
            skLineSegment(sketch, "E1271", {"start": v(-75.66, -4.83) * mm, "end": v(-75.64, -4.68) * mm});
            skLineSegment(sketch, "E1272", {"start": v(-76.08, -5.1) * mm, "end": v(-75.87, -5.07) * mm});
            skLineSegment(sketch, "E1273", {"start": v(-75.87, -5.07) * mm, "end": v(-75.75, -4.98) * mm});
            skLineSegment(sketch, "E1274", {"start": v(-77.68, 4.84) * mm, "end": v(-72.98, 2.66) * mm});
            skLineSegment(sketch, "E1275", {"start": v(-69.59, -6.4) * mm, "end": v(-69.6, -6.6) * mm});
            skLineSegment(sketch, "E1276", {"start": v(-69.6, -6.6) * mm, "end": v(-69.66, -6.78) * mm});
            skLineSegment(sketch, "E1277", {"start": v(-69.66, -6.78) * mm, "end": v(-69.83, -7) * mm});
            skLineSegment(sketch, "E1278", {"start": v(-62.86, 0.05) * mm, "end": v(-70.08, -3.1) * mm});
            skLineSegment(sketch, "E1279", {"start": v(-69.59, -4.51) * mm, "end": v(-69.59, -6.4) * mm});
            skLineSegment(sketch, "E1280", {"start": v(-62.86, 4.44) * mm, "end": v(-62.86, 0.05) * mm});
            skLineSegment(sketch, "E1281", {"start": v(-70.04, -4.51) * mm, "end": v(-69.59, -4.51) * mm});
            skLineSegment(sketch, "E1282", {"start": v(-70.08, 1.1) * mm, "end": v(-62.86, 4.44) * mm});
            skLineSegment(sketch, "E1283", {"start": v(-70.08, -4.76) * mm, "end": v(-70.04, -4.51) * mm});
            skLineSegment(sketch, "E1284", {"start": v(-70.08, -3.1) * mm, "end": v(-70.08, 1.1) * mm});
            skLineSegment(sketch, "E1285", {"start": v(-70.3, -4.55) * mm, "end": v(-70.16, -4.65) * mm});
            skLineSegment(sketch, "E1286", {"start": v(-70.16, -4.65) * mm, "end": v(-70.08, -4.76) * mm});
            skLineSegment(sketch, "E1287", {"start": v(-71.16, 1.1) * mm, "end": v(-78.36, 4.44) * mm});
            skLineSegment(sketch, "E1288", {"start": v(-70.58, -4.48) * mm, "end": v(-70.4, -4.5) * mm});
            skLineSegment(sketch, "E1289", {"start": v(-70.4, -4.5) * mm, "end": v(-70.3, -4.55) * mm});
            skLineSegment(sketch, "E1290", {"start": v(-71.16, -3.14) * mm, "end": v(-71.16, 1.1) * mm});
            skLineSegment(sketch, "E1291", {"start": v(-71.14, -4.76) * mm, "end": v(-71.01, -4.62) * mm});
            skLineSegment(sketch, "E1292", {"start": v(-71.01, -4.62) * mm, "end": v(-70.86, -4.53) * mm});
            skLineSegment(sketch, "E1293", {"start": v(-70.86, -4.53) * mm, "end": v(-70.58, -4.48) * mm});
            skLineSegment(sketch, "E1294", {"start": v(-78.36, 0.07) * mm, "end": v(-71.16, -3.14) * mm});
            skLineSegment(sketch, "E1295", {"start": v(-71.34, -5.5) * mm, "end": v(-71.28, -5.04) * mm});
            skLineSegment(sketch, "E1296", {"start": v(-71.28, -5.04) * mm, "end": v(-71.14, -4.76) * mm});
            skLineSegment(sketch, "E1297", {"start": v(-70.58, -6.5) * mm, "end": v(-70.77, -6.47) * mm});
            skLineSegment(sketch, "E1298", {"start": v(-70.77, -6.47) * mm, "end": v(-70.93, -6.4) * mm});
            skLineSegment(sketch, "E1299", {"start": v(-70.93, -6.4) * mm, "end": v(-71.14, -6.23) * mm});
            skLineSegment(sketch, "E1300", {"start": v(-70.31, -6.43) * mm, "end": v(-70.46, -6.48) * mm});
            skLineSegment(sketch, "E1301", {"start": v(-70.46, -6.48) * mm, "end": v(-70.58, -6.5) * mm});
            skLineSegment(sketch, "E1302", {"start": v(-70.11, -6.27) * mm, "end": v(-70.22, -6.37) * mm});
            skLineSegment(sketch, "E1303", {"start": v(-70.22, -6.37) * mm, "end": v(-70.31, -6.43) * mm});
            skLineSegment(sketch, "E1304", {"start": v(-70.11, -6.4) * mm, "end": v(-70.11, -6.27) * mm});
            skLineSegment(sketch, "E1305", {"start": v(-70.2, -6.72) * mm, "end": v(-70.13, -6.56) * mm});
            skLineSegment(sketch, "E1306", {"start": v(-70.13, -6.56) * mm, "end": v(-70.11, -6.4) * mm});
            skLineSegment(sketch, "E1307", {"start": v(-72.88, -6.45) * mm, "end": v(-72.88, -6.14) * mm});
            skLineSegment(sketch, "E1308", {"start": v(-71.85, -6.45) * mm, "end": v(-72.88, -6.45) * mm});
            skLineSegment(sketch, "E1309", {"start": v(-71.85, -6.14) * mm, "end": v(-71.85, -6.45) * mm});
            skLineSegment(sketch, "E1310", {"start": v(-72.1, -6.09) * mm, "end": v(-71.85, -6.14) * mm});
            skLineSegment(sketch, "E1311", {"start": v(-72.1, -5.14) * mm, "end": v(-72.1, -6.09) * mm});
            skLineSegment(sketch, "E1312", {"start": v(-71.99, -5.01) * mm, "end": v(-72.06, -5.08) * mm});
            skLineSegment(sketch, "E1313", {"start": v(-72.06, -5.08) * mm, "end": v(-72.1, -5.14) * mm});
            skLineSegment(sketch, "E1314", {"start": v(-71.8, -4.97) * mm, "end": v(-71.91, -4.98) * mm});
            skLineSegment(sketch, "E1315", {"start": v(-71.91, -4.98) * mm, "end": v(-71.99, -5.01) * mm});
            skLineSegment(sketch, "E1316", {"start": v(-71.58, -4.98) * mm, "end": v(-71.8, -4.97) * mm});
            skLineSegment(sketch, "E1317", {"start": v(-71.53, -4.5) * mm, "end": v(-71.58, -4.98) * mm});
            skLineSegment(sketch, "E1318", {"start": v(-71.6, -4.48) * mm, "end": v(-71.56, -4.5) * mm});
            skLineSegment(sketch, "E1319", {"start": v(-71.56, -4.5) * mm, "end": v(-71.53, -4.5) * mm});
            skLineSegment(sketch, "E1320", {"start": v(-71.7, -4.48) * mm, "end": v(-71.64, -4.48) * mm});
            skLineSegment(sketch, "E1321", {"start": v(-71.64, -4.48) * mm, "end": v(-71.6, -4.48) * mm});
            skLineSegment(sketch, "E1322", {"start": v(-71.94, -4.56) * mm, "end": v(-71.8, -4.5) * mm});
            skLineSegment(sketch, "E1323", {"start": v(-71.8, -4.5) * mm, "end": v(-71.7, -4.48) * mm});
            skLineSegment(sketch, "E1324", {"start": v(-72.12, -4.8) * mm, "end": v(-72.03, -4.65) * mm});
            skLineSegment(sketch, "E1325", {"start": v(-72.03, -4.65) * mm, "end": v(-71.94, -4.56) * mm});
            skLineSegment(sketch, "E1326", {"start": v(-72.14, -4.51) * mm, "end": v(-72.12, -4.8) * mm});
            skLineSegment(sketch, "E1327", {"start": v(-72.9, -4.51) * mm, "end": v(-72.14, -4.51) * mm});
            skLineSegment(sketch, "E1328", {"start": v(-72.9, -4.83) * mm, "end": v(-72.9, -4.51) * mm});
            skLineSegment(sketch, "E1329", {"start": v(-72.63, -4.88) * mm, "end": v(-72.9, -4.83) * mm});
            skLineSegment(sketch, "E1330", {"start": v(-72.63, -6.09) * mm, "end": v(-72.63, -4.88) * mm});
            skLineSegment(sketch, "E1331", {"start": v(-72.88, -6.14) * mm, "end": v(-72.63, -6.09) * mm});
            skLineSegment(sketch, "E1332", {"start": v(-74.33, -6.05) * mm, "end": v(-74.24, -6.1) * mm});
            skLineSegment(sketch, "E1333", {"start": v(-74.24, -6.1) * mm, "end": v(-74.15, -6.1) * mm});
            skCircle(sketch, "E1334", {"center": v(-32.29, 0) * mm, "radius": 11.5 * mm});
            skCircle(sketch, "E1335", {"center": v(-32.29, 0) * mm, "radius": 10.5 * mm});
            skArc(sketch, "E1336", {"start": v(-36.7, 7.64) * mm, "mid": v(-32.29, -8.83) * mm, "end": v(-27.87, 7.64) * mm});
            skArc(sketch, "E1337", {"start": v(-35.85, 6.17) * mm, "mid": v(-32.29, -7.12) * mm, "end": v(-28.72, 6.17) * mm});
            skPoint(sketch, "E1338.orphan", {"position": v(-32.29, 1.5) * mm});
            skArc(sketch, "E1339", {"start": v(-36.7, 7.64) * mm, "mid": v(-35.54, 7.33) * mm, "end": v(-35.85, 6.17) * mm});
            skArc(sketch, "E1340", {"start": v(-27.87, 7.64) * mm, "mid": v(-29.03, 7.33) * mm, "end": v(-28.72, 6.17) * mm});
            skLineSegment(sketch, "E1341.left", {"start": v(-34.29, 6.76) * mm, "end": v(-34.29, -3.24) * mm});
            skLineSegment(sketch, "E1342.MirrorCS", {"start": v(-30.29, 6.76) * mm, "end": v(-30.29, -3.24) * mm});
            skArc(sketch, "E1343", {"start": v(-34.29, 6.76) * mm, "mid": v(-32.29, 8.76) * mm, "end": v(-30.29, 6.76) * mm});
            skArc(sketch, "E1344", {"start": v(-30.29, -3.24) * mm, "mid": v(-32.29, -5.24) * mm, "end": v(-34.29, -3.24) * mm});
            const initialGuessF3  = {"E1054": [0.02675, -0.00385, 1, 0, 0.0077]};
            skSetInitialGuess(sketch, initialGuessF3);
            skSolve(sketch);
        }
        {
            var Q0;
            Q0=makeQuery(id+"F3.imprint","IMPRINT",FACE,{"disambiguationData":[TD([[makeQuery(id+"F3.imprint","IMPRINT",EDGE,{"derivedFrom":sQuery(id+"F3.wireOp",EDGE,"E1054.sketch_text.stroke-0")}),-1.0]])]});
            var Q1;
            Q1=makeQuery(id+"F3.imprint","IMPRINT",FACE,{"disambiguationData":[TD([[makeQuery(id+"F3.imprint","IMPRINT",EDGE,{"derivedFrom":sQuery(id+"F3.wireOp",EDGE,"E1054.sketch_text.stroke-6")}),-1.0]])]});
            var Q2;
            Q2=makeQuery(id+"F3.imprint","IMPRINT",FACE,{"disambiguationData":[TD([[makeQuery(id+"F3.imprint","IMPRINT",EDGE,{"derivedFrom":sQuery(id+"F3.wireOp",EDGE,"E1071")}),1.0]])]});
            var Q3;
            Q3=makeQuery(id+"F3.imprint","IMPRINT",FACE,{"disambiguationData":[TD([[makeQuery(id+"F3.imprint","IMPRINT",EDGE,{"derivedFrom":sQuery(id+"F3.wireOp",EDGE,"E1116")}),-1.0]])]});
            var Q4;
            Q4=makeQuery(id+"F3.imprint","IMPRINT",FACE,{"disambiguationData":[TD([[makeQuery(id+"F3.imprint","IMPRINT",EDGE,{"derivedFrom":sQuery(id+"F3.wireOp",EDGE,"E1126")}),-1.0]])]});
            var Q5;
            Q5=makeQuery(id+"F3.imprint","IMPRINT",FACE,{"disambiguationData":[TD([[makeQuery(id+"F3.imprint","IMPRINT",EDGE,{"derivedFrom":sQuery(id+"F3.wireOp",EDGE,"E1130")}),-1.0]])]});
            var Q6;
            Q6=makeQuery(id+"F3.imprint","IMPRINT",FACE,{"disambiguationData":[TD([[makeQuery(id+"F3.imprint","IMPRINT",EDGE,{"derivedFrom":sQuery(id+"F3.wireOp",EDGE,"E1187")}),1.0]])]});
            var Q7;
            Q7=makeQuery(id+"F3.imprint","IMPRINT",FACE,{"disambiguationData":[TD([[makeQuery(id+"F3.imprint","IMPRINT",EDGE,{"derivedFrom":sQuery(id+"F3.wireOp",EDGE,"E1237")}),1.0]])]});
            var Q8;
            Q8=makeQuery(id+"F3.imprint","IMPRINT",FACE,{"disambiguationData":[TD([[makeQuery(id+"F3.imprint","IMPRINT",EDGE,{"derivedFrom":sQuery(id+"F3.wireOp",EDGE,"E1278")}),-1.0]])]});
            var Q9;
            Q9=makeQuery(id+"F3.imprint","IMPRINT",FACE,{"disambiguationData":[TD([[makeQuery(id+"F3.imprint","IMPRINT",EDGE,{"derivedFrom":sQuery(id+"F3.wireOp",EDGE,"E1307")}),-1.0]])]});
            var Q10;
            Q10=makeQuery(id+"F3.imprint","IMPRINT",FACE,{"disambiguationData":[TD([[makeQuery(id+"F3.imprint","IMPRINT",EDGE,{"derivedFrom":sQuery(id+"F3.wireOp",EDGE,"E1054.sketch_text.stroke-18")}),-1.0]])]});
            var Q11;
            Q11=makeQuery(id+"F3.imprint","IMPRINT",FACE,{"disambiguationData":[TD([[makeQuery(id+"F3.imprint","IMPRINT",EDGE,{"derivedFrom":sQuery(id+"F3.wireOp",EDGE,"E1072")}),-1.0]])]});
            var Q12;
            Q12=makeQuery(id+"F3.imprint","IMPRINT",FACE,{"disambiguationData":[TD([[makeQuery(id+"F3.imprint","IMPRINT",EDGE,{"derivedFrom":sQuery(id+"F3.wireOp",EDGE,"E1140")}),-1.0]])]});
            var Q13;
            Q13=makeQuery(id+"F3.imprint","IMPRINT",FACE,{"disambiguationData":[TD([[makeQuery(id+"F3.imprint","IMPRINT",EDGE,{"derivedFrom":sQuery(id+"F3.wireOp",EDGE,"E1158")}),-1.0]])]});
            var Q14;
            Q14=makeQuery(id+"F3.imprint","IMPRINT",FACE,{"disambiguationData":[TD([[makeQuery(id+"F3.imprint","IMPRINT",EDGE,{"derivedFrom":sQuery(id+"F3.wireOp",EDGE,"E1196")}),-1.0]])]});
            var Q15;
            Q15=makeQuery(id+"F3.imprint","IMPRINT",FACE,{"disambiguationData":[TD([[makeQuery(id+"F3.imprint","IMPRINT",EDGE,{"derivedFrom":sQuery(id+"F3.wireOp",EDGE,"E7")}),-1.0]])]});
            var Q16;
            Q16=makeQuery(id+"F3.imprint","IMPRINT",FACE,{"disambiguationData":[TD([[makeQuery(id+"F3.imprint","IMPRINT",EDGE,{"derivedFrom":sQuery(id+"F3.wireOp",EDGE,"E1335")}),1.0]])]});
            var Q17;
            {var subQ1=sQuery(id+"F3.wireOp",EDGE,"E1057");Q17=makeQuery(id+"F3.imprint","IMPRINT",FACE,{"disambiguationData":[TD([[makeQuery(id+"F3.imprint","IMPRINT",EDGE,{"derivedFrom":subQ1}),-1.0]])]});}
            var Q18;
            Q18=makeQuery(id+"F3.imprint","IMPRINT",FACE,{"disambiguationData":[TD([[makeQuery(id+"F3.imprint","IMPRINT",EDGE,{"derivedFrom":sQuery(id+"F3.wireOp",EDGE,"E1056")}),1.0]])]});
            extrude(context, id + "F4", {"entities" : qUnion([Q0, Q1, Q2, Q3, Q4, Q5, Q6, Q7, Q8, Q9, Q10, Q11, Q12, Q13, Q14, Q15, Q16, Q17, Q18]), "operationType" : NewBodyOperationType.REMOVE, "oppositeDirection" : true, "depth" : 2 * mm, "offsetDistance" : 25 * mm});
        }
    });
